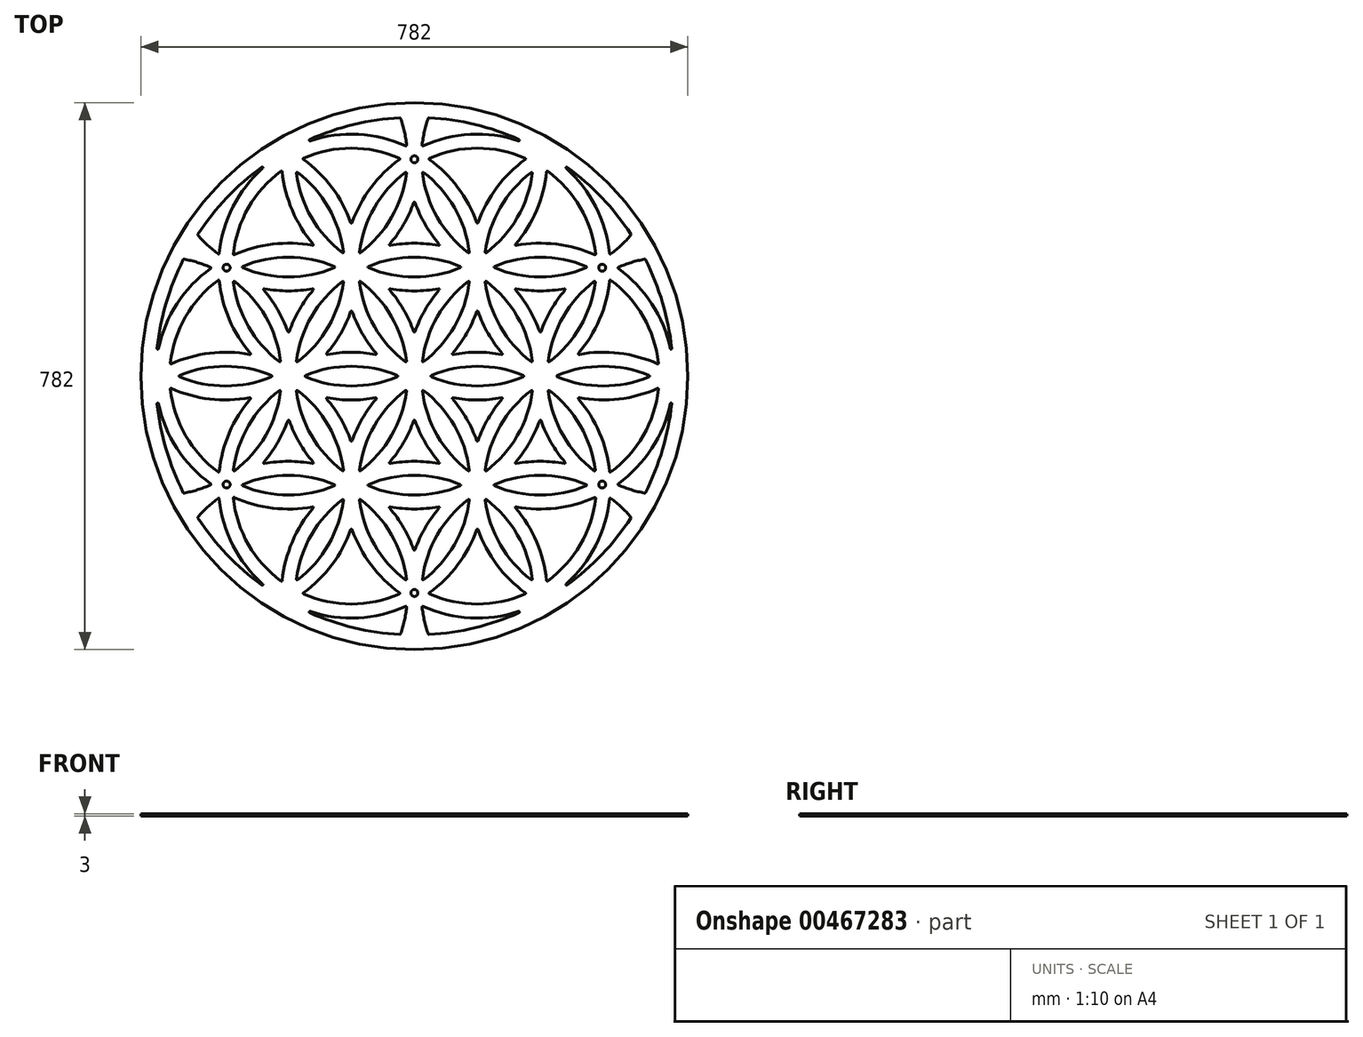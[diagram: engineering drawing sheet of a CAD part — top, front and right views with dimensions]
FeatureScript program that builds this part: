
annotation { "Feature Type Name" : "Feature", "Feature Type Description" : "" }
export const myFeature = defineFeature(function(context is Context, id is Id, definition is map)
    precondition{}
    {
        {
            var Q0;
            Q0=qCreatedBy(makeId("Top.planeOp"),FACE);
            var sketch = newSketch(context, id + "F0", { "sketchPlane" : qUnion([Q0])});
            skArc(sketch, "E0", {"start": v(-280.58, 137.05) * mm, "mid": v(-327.22, 85) * mm, "end": v(-348.98, 18.58) * mm});
            skArc(sketch, "E1", {"start": v(-291.41, 153.9) * mm, "mid": v(-339.34, 103.5) * mm, "end": v(-365.91, 39.2) * mm});
            skArc(sketch, "E2", {"start": v(-190.58, 292.94) * mm, "mid": v(-237.22, 240.88) * mm, "end": v(-258.98, 174.46) * mm});
            skArc(sketch, "E3", {"start": v(-21.41, 309.8) * mm, "mid": v(-62.1, 269.75) * mm, "end": v(-89.06, 219.43) * mm});
            skArc(sketch, "E4", {"start": v(257.58, 173.44) * mm, "mid": v(202.56, 188.66) * mm, "end": v(145.5, 186.84) * mm});
            skArc(sketch, "E5", {"start": v(179.06, 63.55) * mm, "mid": v(164.54, 95) * mm, "end": v(144.56, 123.3) * mm});
            skArc(sketch, "E6", {"start": v(-234.56, -32.6) * mm, "mid": v(-264.66, -81.1) * mm, "end": v(-279, -136.35) * mm});
            skArc(sketch, "E7", {"start": v(-192.97, -20.62) * mm, "mid": v(-237.22, -70.88) * mm, "end": v(-258.63, -134.35) * mm});
            skArc(sketch, "E8", {"start": v(155.66, 0.92) * mm, "mid": v(90, 14.12) * mm, "end": v(24.34, 0.92) * mm});
            skCircle(sketch, "E9", {"center": v(0, 0) * mm, "radius": 412 * mm});
            skArc(sketch, "E10", {"start": v(329.26, 167.2) * mm, "mid": v(310.1, 162.5) * mm, "end": v(291.6, 155.63) * mm});
            skArc(sketch, "E11", {"start": v(309.43, -201.55) * mm, "mid": v(295.78, -187.3) * mm, "end": v(280.58, -174.72) * mm});
            skArc(sketch, "E12", {"start": v(-214.5, 124.93) * mm, "mid": v(-180, 121.77) * mm, "end": v(-145.5, 124.93) * mm});
            skArc(sketch, "E13", {"start": v(-309.43, 201.55) * mm, "mid": v(-295.78, 187.3) * mm, "end": v(-280.58, 174.72) * mm});
            skArc(sketch, "E14", {"start": v(19.83, 368.75) * mm, "mid": v(14.3, 349.8) * mm, "end": v(11.02, 330.35) * mm});
            skArc(sketch, "E15", {"start": v(-20.83, 369.41) * mm, "mid": v(-86.68, 359.7) * mm, "end": v(-149.71, 338.36) * mm});
            skArc(sketch, "E16.trimOffspring", {"start": v(-329.26, -167.2) * mm, "mid": v(-310.1, -162.5) * mm, "end": v(-291.6, -155.63) * mm});
            skArc(sketch, "E17.trimOffspring", {"start": v(-19.83, -368.75) * mm, "mid": v(-14.3, -349.8) * mm, "end": v(-11.02, -330.35) * mm});
            skArc(sketch, "E18.trimOffspring", {"start": v(-189, 292.24) * mm, "mid": v(-174.66, 236.98) * mm, "end": v(-144.56, 188.47) * mm});
            skArc(sketch, "E19.trimOffspring", {"start": v(-12.42, 329.32) * mm, "mid": v(-80.04, 345.62) * mm, "end": v(-149, 336.5) * mm});
            skArc(sketch, "E20.trimOffspring", {"start": v(-11.02, 330.35) * mm, "mid": v(-14.3, 349.8) * mm, "end": v(-19.83, 368.75) * mm});
            skArc(sketch, "E21.trimOffspring", {"start": v(0.94, 248.22) * mm, "mid": v(15.46, 216.77) * mm, "end": v(35.44, 188.47) * mm});
            skArc(sketch, "E22.trimOffspring", {"start": v(-21.6, 311.52) * mm, "mid": v(-90, 325.88) * mm, "end": v(-158.4, 311.52) * mm});
            skArc(sketch, "E23.trimOffspring", {"start": v(11.37, 290.23) * mm, "mid": v(32.78, 226.77) * mm, "end": v(77.03, 176.5) * mm});
            skArc(sketch, "E24.trimOffspring", {"start": v(-12.97, 291.15) * mm, "mid": v(-57.22, 240.88) * mm, "end": v(-78.63, 177.42) * mm});
            skArc(sketch, "E25.trimOffspring", {"start": v(158.59, 309.8) * mm, "mid": v(117.9, 269.75) * mm, "end": v(90.94, 219.43) * mm});
            skArc(sketch, "E26.trimOffspring", {"start": v(167.03, 291.15) * mm, "mid": v(122.78, 240.88) * mm, "end": v(101.37, 177.42) * mm});
            skArc(sketch, "E27.trimOffspring", {"start": v(158.4, 311.52) * mm, "mid": v(90, 325.88) * mm, "end": v(21.6, 311.52) * mm});
            skArc(sketch, "E28.trimOffspring", {"start": v(-279, 136.35) * mm, "mid": v(-264.66, 81.1) * mm, "end": v(-234.56, 32.6) * mm});
            skArc(sketch, "E29.trimOffspring", {"start": v(-291.6, 155.63) * mm, "mid": v(-310.1, 162.5) * mm, "end": v(-329.26, 167.2) * mm});
            skArc(sketch, "E30.trimOffspring", {"start": v(-258.63, 134.35) * mm, "mid": v(-237.22, 70.88) * mm, "end": v(-192.97, 20.62) * mm});
            skArc(sketch, "E31.trimOffspring", {"start": v(-245.66, 154.96) * mm, "mid": v(-180, 141.77) * mm, "end": v(-114.34, 154.96) * mm});
            skArc(sketch, "E32.trimOffspring", {"start": v(280.58, 174.72) * mm, "mid": v(295.78, 187.3) * mm, "end": v(309.43, 201.55) * mm});
            skArc(sketch, "E33.trimOffspring", {"start": v(279, 175.42) * mm, "mid": v(259.3, 242.13) * mm, "end": v(216.91, 297.28) * mm});
            skArc(sketch, "E34.trimOffspring", {"start": v(257.03, 135.27) * mm, "mid": v(212.78, 85) * mm, "end": v(191.37, 21.54) * mm});
            skArc(sketch, "E35.trimOffspring", {"start": v(245.66, 156.8) * mm, "mid": v(180, 170) * mm, "end": v(114.34, 156.8) * mm});
            skArc(sketch, "E36.trimOffspring", {"start": v(215.44, 123.3) * mm, "mid": v(195.46, 95) * mm, "end": v(180.94, 63.55) * mm});
            skArc(sketch, "E37.trimOffspring", {"start": v(258.98, 174.46) * mm, "mid": v(237.22, 240.88) * mm, "end": v(190.58, 292.94) * mm});
            skArc(sketch, "E38.trimOffspring", {"start": v(235.5, -30.96) * mm, "mid": v(292.56, -32.77) * mm, "end": v(347.58, -17.56) * mm});
            skArc(sketch, "E39.trimOffspring", {"start": v(204.34, -0.92) * mm, "mid": v(270, -14.12) * mm, "end": v(335.66, -0.92) * mm});
            skArc(sketch, "E40.trimOffspring", {"start": v(234.56, 32.6) * mm, "mid": v(264.66, 81.1) * mm, "end": v(279, 136.35) * mm});
            skArc(sketch, "E41.trimOffspring", {"start": v(180.94, -63.55) * mm, "mid": v(195.46, -95) * mm, "end": v(215.44, -123.3) * mm});
            skArc(sketch, "E42.trimOffspring", {"start": v(192.97, 20.62) * mm, "mid": v(237.22, 70.88) * mm, "end": v(258.63, 134.35) * mm});
            skArc(sketch, "E43.trimOffspring", {"start": v(124.5, 30.96) * mm, "mid": v(90, 34.12) * mm, "end": v(55.5, 30.96) * mm});
            skArc(sketch, "E44.trimOffspring", {"start": v(125.44, -32.6) * mm, "mid": v(105.46, -60.88) * mm, "end": v(90.94, -92.34) * mm});
            skArc(sketch, "E45.trimOffspring", {"start": v(167.03, -20.62) * mm, "mid": v(122.78, -70.88) * mm, "end": v(101.37, -134.35) * mm});
            skArc(sketch, "E46.trimOffspring", {"start": v(168.63, 21.54) * mm, "mid": v(147.22, 85) * mm, "end": v(102.97, 135.27) * mm});
            skArc(sketch, "E47.trimOffspring", {"start": v(191.37, -21.54) * mm, "mid": v(212.78, -85) * mm, "end": v(257.03, -135.27) * mm});
            skArc(sketch, "E48.trimOffspring", {"start": v(145.5, 124.93) * mm, "mid": v(180, 121.77) * mm, "end": v(214.5, 124.93) * mm});
            skArc(sketch, "E49.trimOffspring", {"start": v(-348.98, -18.58) * mm, "mid": v(-327.22, -85) * mm, "end": v(-280.58, -137.05) * mm});
            skArc(sketch, "E50.trimOffspring", {"start": v(-335.66, -0.92) * mm, "mid": v(-270, -14.12) * mm, "end": v(-204.34, -0.92) * mm});
            skArc(sketch, "E51.trimOffspring", {"start": v(-347.58, -17.56) * mm, "mid": v(-292.56, -32.77) * mm, "end": v(-235.5, -30.96) * mm});
            skArc(sketch, "E52.trimOffspring", {"start": v(-365.91, -39.2) * mm, "mid": v(-339.34, -103.5) * mm, "end": v(-291.41, -153.9) * mm});
            skArc(sketch, "E53.trimOffspring", {"start": v(-145.5, 186.84) * mm, "mid": v(-202.56, 188.66) * mm, "end": v(-257.58, 173.44) * mm});
            skArc(sketch, "E54.trimOffspring", {"start": v(-77.03, 176.5) * mm, "mid": v(-32.78, 226.77) * mm, "end": v(-11.37, 290.23) * mm});
            skArc(sketch, "E55.trimOffspring", {"start": v(-168.63, 290.23) * mm, "mid": v(-147.22, 226.77) * mm, "end": v(-102.97, 176.5) * mm});
            skArc(sketch, "E56.trimOffspring", {"start": v(-34.5, 124.93) * mm, "mid": v(0, 121.77) * mm, "end": v(34.5, 124.93) * mm});
            skArc(sketch, "E57.trimOffspring", {"start": v(-78.63, 134.35) * mm, "mid": v(-57.22, 70.88) * mm, "end": v(-12.97, 20.62) * mm});
            skArc(sketch, "E58.trimOffspring", {"start": v(-89.06, 92.34) * mm, "mid": v(-74.54, 60.88) * mm, "end": v(-54.56, 32.6) * mm});
            skArc(sketch, "E59.trimOffspring", {"start": v(-102.97, 135.27) * mm, "mid": v(-147.22, 85) * mm, "end": v(-168.63, 21.54) * mm});
            skArc(sketch, "E60.trimOffspring", {"start": v(-114.34, 156.8) * mm, "mid": v(-180, 170) * mm, "end": v(-245.66, 156.8) * mm});
            skArc(sketch, "E61.trimOffspring", {"start": v(-144.56, 123.3) * mm, "mid": v(-164.54, 95) * mm, "end": v(-179.06, 63.55) * mm});
            skArc(sketch, "E62.trimOffspring", {"start": v(-180.94, 63.55) * mm, "mid": v(-195.46, 95) * mm, "end": v(-215.44, 123.3) * mm});
            skArc(sketch, "E63.trimOffspring", {"start": v(-35.44, 188.47) * mm, "mid": v(-15.46, 216.77) * mm, "end": v(-0.94, 248.22) * mm});
            skArc(sketch, "E64.trimOffspring", {"start": v(34.5, 186.84) * mm, "mid": v(0, 190) * mm, "end": v(-34.5, 186.84) * mm});
            skArc(sketch, "E65.trimOffspring", {"start": v(-90.94, 219.43) * mm, "mid": v(-117.9, 269.75) * mm, "end": v(-158.59, 309.8) * mm});
            skArc(sketch, "E66.trimOffspring", {"start": v(-101.37, 177.42) * mm, "mid": v(-122.78, 240.88) * mm, "end": v(-167.03, 291.15) * mm});
            skArc(sketch, "E67.trimOffspring", {"start": v(-65.66, 154.96) * mm, "mid": v(0, 141.77) * mm, "end": v(65.66, 154.96) * mm});
            skArc(sketch, "E68.trimOffspring", {"start": v(-216.91, 297.28) * mm, "mid": v(-259.3, 242.13) * mm, "end": v(-279, 175.42) * mm});
            skArc(sketch, "E69.trimOffspring", {"start": v(-218.17, 298.84) * mm, "mid": v(-268.18, 254.92) * mm, "end": v(-309.5, 202.75) * mm});
            skArc(sketch, "E70.trimOffspring", {"start": v(-330.34, 166.67) * mm, "mid": v(-354.85, 104.79) * mm, "end": v(-367.88, 39.52) * mm});
            skArc(sketch, "E71.trimOffspring", {"start": v(149, 336.5) * mm, "mid": v(80.04, 345.62) * mm, "end": v(12.42, 329.32) * mm});
            skArc(sketch, "E72.trimOffspring", {"start": v(149.71, 338.36) * mm, "mid": v(86.68, 359.7) * mm, "end": v(20.83, 369.41) * mm});
            skArc(sketch, "E73.trimOffspring", {"start": v(309.5, 202.75) * mm, "mid": v(268.18, 254.92) * mm, "end": v(218.17, 298.84) * mm});
            skArc(sketch, "E74.trimOffspring", {"start": v(90.94, 92.34) * mm, "mid": v(105.46, 60.88) * mm, "end": v(125.44, 32.6) * mm});
            skArc(sketch, "E75.trimOffspring", {"start": v(35.44, 123.3) * mm, "mid": v(15.46, 95) * mm, "end": v(0.94, 63.55) * mm});
            skArc(sketch, "E76.trimOffspring", {"start": v(89.06, 219.43) * mm, "mid": v(62.1, 269.75) * mm, "end": v(21.41, 309.8) * mm});
            skArc(sketch, "E77.trimOffspring", {"start": v(144.56, 188.47) * mm, "mid": v(174.66, 236.98) * mm, "end": v(189, 292.24) * mm});
            skArc(sketch, "E78.trimOffspring", {"start": v(102.97, 176.5) * mm, "mid": v(147.22, 226.77) * mm, "end": v(168.63, 290.23) * mm});
            skArc(sketch, "E79.trimOffspring", {"start": v(78.63, 177.42) * mm, "mid": v(57.22, 240.88) * mm, "end": v(12.97, 291.15) * mm});
            skArc(sketch, "E80.trimOffspring", {"start": v(114.34, 154.96) * mm, "mid": v(180, 141.77) * mm, "end": v(245.66, 154.96) * mm});
            skArc(sketch, "E81.trimOffspring", {"start": v(101.37, 134.35) * mm, "mid": v(122.78, 70.88) * mm, "end": v(167.03, 20.62) * mm});
            skArc(sketch, "E82.trimOffspring", {"start": v(77.03, 135.27) * mm, "mid": v(32.78, 85) * mm, "end": v(11.37, 21.54) * mm});
            skArc(sketch, "E83.trimOffspring", {"start": v(65.66, 156.8) * mm, "mid": v(0, 170) * mm, "end": v(-65.66, 156.8) * mm});
            skArc(sketch, "E84.trimOffspring", {"start": v(-367.88, -39.52) * mm, "mid": v(-354.85, -104.79) * mm, "end": v(-330.34, -166.67) * mm});
            skArc(sketch, "E85.trimOffspring", {"start": v(-235.5, 30.96) * mm, "mid": v(-292.56, 32.77) * mm, "end": v(-347.58, 17.56) * mm});
            skArc(sketch, "E86.trimOffspring", {"start": v(-124.5, -30.96) * mm, "mid": v(-90, -34.12) * mm, "end": v(-55.5, -30.96) * mm});
            skArc(sketch, "E87.trimOffspring", {"start": v(-179.06, -63.55) * mm, "mid": v(-164.54, -95) * mm, "end": v(-144.56, -123.3) * mm});
            skArc(sketch, "E88.trimOffspring", {"start": v(-125.44, 32.6) * mm, "mid": v(-105.46, 60.88) * mm, "end": v(-90.94, 92.34) * mm});
            skArc(sketch, "E89.trimOffspring", {"start": v(-204.34, 0.92) * mm, "mid": v(-270, 14.12) * mm, "end": v(-335.66, 0.92) * mm});
            skArc(sketch, "E90.trimOffspring", {"start": v(-191.37, 21.54) * mm, "mid": v(-212.78, 85) * mm, "end": v(-257.03, 135.27) * mm});
            skArc(sketch, "E91.trimOffspring", {"start": v(-167.03, 20.62) * mm, "mid": v(-122.78, 70.88) * mm, "end": v(-101.37, 134.35) * mm});
            skArc(sketch, "E92.trimOffspring", {"start": v(-155.66, -0.92) * mm, "mid": v(-90, -14.12) * mm, "end": v(-24.34, -0.92) * mm});
            skArc(sketch, "E93.trimOffspring", {"start": v(-168.63, -21.54) * mm, "mid": v(-147.22, -85) * mm, "end": v(-102.97, -135.27) * mm});
            skArc(sketch, "E94.trimOffspring", {"start": v(335.66, 0.92) * mm, "mid": v(270, 14.12) * mm, "end": v(204.34, 0.92) * mm});
            skArc(sketch, "E95.trimOffspring", {"start": v(347.58, 17.56) * mm, "mid": v(292.56, 32.77) * mm, "end": v(235.5, 30.96) * mm});
            skArc(sketch, "E96.trimOffspring", {"start": v(348.98, 18.58) * mm, "mid": v(327.22, 85) * mm, "end": v(280.58, 137.05) * mm});
            skArc(sketch, "E97.trimOffspring", {"start": v(365.91, 39.2) * mm, "mid": v(339.34, 103.5) * mm, "end": v(291.41, 153.9) * mm});
            skArc(sketch, "E98.trimOffspring", {"start": v(367.88, 39.52) * mm, "mid": v(354.85, 104.79) * mm, "end": v(330.34, 166.67) * mm});
            skArc(sketch, "E99.trimOffspring", {"start": v(-11.37, 21.54) * mm, "mid": v(-32.78, 85) * mm, "end": v(-77.03, 135.27) * mm});
            skArc(sketch, "E100.trimOffspring", {"start": v(-0.94, 63.55) * mm, "mid": v(-15.46, 95) * mm, "end": v(-35.44, 123.3) * mm});
            skArc(sketch, "E101.trimOffspring", {"start": v(12.97, 20.62) * mm, "mid": v(57.22, 70.88) * mm, "end": v(78.63, 134.35) * mm});
            skArc(sketch, "E102.trimOffspring", {"start": v(54.56, 32.6) * mm, "mid": v(74.54, 60.88) * mm, "end": v(89.06, 92.34) * mm});
            skArc(sketch, "E103.trimOffspring", {"start": v(24.34, -0.92) * mm, "mid": v(90, -14.12) * mm, "end": v(155.66, -0.92) * mm});
            skArc(sketch, "E104.trimOffspring", {"start": v(55.5, -30.96) * mm, "mid": v(90, -34.12) * mm, "end": v(124.5, -30.96) * mm});
            skArc(sketch, "E105.trimOffspring", {"start": v(0.94, -63.55) * mm, "mid": v(15.46, -95) * mm, "end": v(35.44, -123.3) * mm});
            skArc(sketch, "E106.trimOffspring", {"start": v(11.37, -21.54) * mm, "mid": v(32.78, -85) * mm, "end": v(77.03, -135.27) * mm});
            skArc(sketch, "E107.trimOffspring", {"start": v(-12.97, -20.62) * mm, "mid": v(-57.22, -70.88) * mm, "end": v(-78.63, -134.35) * mm});
            skArc(sketch, "E108.trimOffspring", {"start": v(-54.56, -32.6) * mm, "mid": v(-74.54, -60.88) * mm, "end": v(-89.06, -92.34) * mm});
            skArc(sketch, "E109.trimOffspring", {"start": v(-24.34, 0.92) * mm, "mid": v(-90, 14.12) * mm, "end": v(-155.66, 0.92) * mm});
            skArc(sketch, "E110.trimOffspring", {"start": v(-55.5, 30.96) * mm, "mid": v(-90, 34.12) * mm, "end": v(-124.5, 30.96) * mm});
            skArc(sketch, "E111.trimOffspring", {"start": v(-309.5, -202.75) * mm, "mid": v(-268.18, -254.92) * mm, "end": v(-218.17, -298.84) * mm});
            skArc(sketch, "E112.trimOffspring", {"start": v(-279, -175.42) * mm, "mid": v(-259.3, -242.13) * mm, "end": v(-216.91, -297.28) * mm});
            skArc(sketch, "E113.trimOffspring", {"start": v(-280.58, -174.72) * mm, "mid": v(-295.78, -187.3) * mm, "end": v(-309.43, -201.55) * mm});
            skArc(sketch, "E114.trimOffspring", {"start": v(-215.44, -123.3) * mm, "mid": v(-195.46, -95) * mm, "end": v(-180.94, -63.55) * mm});
            skArc(sketch, "E115.trimOffspring", {"start": v(-257.03, -135.27) * mm, "mid": v(-212.78, -85) * mm, "end": v(-191.37, -21.54) * mm});
            skArc(sketch, "E116.trimOffspring", {"start": v(-257.58, -173.44) * mm, "mid": v(-202.56, -188.66) * mm, "end": v(-145.5, -186.84) * mm});
            skArc(sketch, "E117.trimOffspring", {"start": v(-258.98, -174.46) * mm, "mid": v(-237.22, -240.88) * mm, "end": v(-190.58, -292.94) * mm});
            skArc(sketch, "E118.trimOffspring", {"start": v(-245.66, -156.8) * mm, "mid": v(-180, -170) * mm, "end": v(-114.34, -156.8) * mm});
            skArc(sketch, "E119.trimOffspring", {"start": v(-167.03, -291.15) * mm, "mid": v(-122.78, -240.88) * mm, "end": v(-101.37, -177.42) * mm});
            skArc(sketch, "E120.trimOffspring", {"start": v(-149, -336.5) * mm, "mid": v(-80.04, -345.62) * mm, "end": v(-12.42, -329.32) * mm});
            skArc(sketch, "E121.trimOffspring", {"start": v(-149.71, -338.36) * mm, "mid": v(-86.68, -359.7) * mm, "end": v(-20.83, -369.41) * mm});
            skArc(sketch, "E122.trimOffspring", {"start": v(-158.59, -309.8) * mm, "mid": v(-117.9, -269.75) * mm, "end": v(-90.94, -219.43) * mm});
            skArc(sketch, "E123.trimOffspring", {"start": v(-158.4, -311.52) * mm, "mid": v(-90, -325.88) * mm, "end": v(-21.6, -311.52) * mm});
            skArc(sketch, "E124.trimOffspring", {"start": v(-114.34, -154.96) * mm, "mid": v(-180, -141.77) * mm, "end": v(-245.66, -154.96) * mm});
            skArc(sketch, "E125.trimOffspring", {"start": v(-145.5, -124.93) * mm, "mid": v(-180, -121.77) * mm, "end": v(-214.5, -124.93) * mm});
            skArc(sketch, "E126.trimOffspring", {"start": v(-101.37, -134.35) * mm, "mid": v(-122.78, -70.88) * mm, "end": v(-167.03, -20.62) * mm});
            skArc(sketch, "E127.trimOffspring", {"start": v(-90.94, -92.34) * mm, "mid": v(-105.46, -60.88) * mm, "end": v(-125.44, -32.6) * mm});
            skArc(sketch, "E128.trimOffspring", {"start": v(-77.03, -135.27) * mm, "mid": v(-32.78, -85) * mm, "end": v(-11.37, -21.54) * mm});
            skArc(sketch, "E129.trimOffspring", {"start": v(-35.44, -123.3) * mm, "mid": v(-15.46, -95) * mm, "end": v(-0.94, -63.55) * mm});
            skArc(sketch, "E130.trimOffspring", {"start": v(-65.66, -156.8) * mm, "mid": v(0, -170) * mm, "end": v(65.66, -156.8) * mm});
            skArc(sketch, "E131.trimOffspring", {"start": v(-34.5, -186.84) * mm, "mid": v(0, -190) * mm, "end": v(34.5, -186.84) * mm});
            skArc(sketch, "E132.trimOffspring", {"start": v(-78.63, -177.42) * mm, "mid": v(-57.22, -240.88) * mm, "end": v(-12.97, -291.15) * mm});
            skArc(sketch, "E133.trimOffspring", {"start": v(-89.06, -219.43) * mm, "mid": v(-62.1, -269.75) * mm, "end": v(-21.41, -309.8) * mm});
            skArc(sketch, "E134.trimOffspring", {"start": v(-102.97, -176.5) * mm, "mid": v(-147.22, -226.77) * mm, "end": v(-168.63, -290.23) * mm});
            skArc(sketch, "E135.trimOffspring", {"start": v(-144.56, -188.47) * mm, "mid": v(-174.66, -236.98) * mm, "end": v(-189, -292.24) * mm});
            skArc(sketch, "E136.trimOffspring", {"start": v(65.66, -154.96) * mm, "mid": v(0, -141.77) * mm, "end": v(-65.66, -154.96) * mm});
            skArc(sketch, "E137.trimOffspring", {"start": v(34.5, -124.93) * mm, "mid": v(0, -121.77) * mm, "end": v(-34.5, -124.93) * mm});
            skArc(sketch, "E138.trimOffspring", {"start": v(78.63, -134.35) * mm, "mid": v(57.22, -70.88) * mm, "end": v(12.97, -20.62) * mm});
            skArc(sketch, "E139.trimOffspring", {"start": v(89.06, -92.34) * mm, "mid": v(74.54, -60.88) * mm, "end": v(54.56, -32.6) * mm});
            skArc(sketch, "E140.trimOffspring", {"start": v(102.97, -135.27) * mm, "mid": v(147.22, -85) * mm, "end": v(168.63, -21.54) * mm});
            skArc(sketch, "E141.trimOffspring", {"start": v(144.56, -123.3) * mm, "mid": v(164.54, -95) * mm, "end": v(179.06, -63.55) * mm});
            skArc(sketch, "E142.trimOffspring", {"start": v(114.34, -156.8) * mm, "mid": v(180, -170) * mm, "end": v(245.66, -156.8) * mm});
            skArc(sketch, "E143.trimOffspring", {"start": v(145.5, -186.84) * mm, "mid": v(202.56, -188.66) * mm, "end": v(257.58, -173.44) * mm});
            skArc(sketch, "E144.trimOffspring", {"start": v(101.37, -177.42) * mm, "mid": v(122.78, -240.88) * mm, "end": v(167.03, -291.15) * mm});
            skArc(sketch, "E145.trimOffspring", {"start": v(90.94, -219.43) * mm, "mid": v(117.9, -269.75) * mm, "end": v(158.59, -309.8) * mm});
            skArc(sketch, "E146.trimOffspring", {"start": v(77.03, -176.5) * mm, "mid": v(32.78, -226.77) * mm, "end": v(11.37, -290.23) * mm});
            skArc(sketch, "E147.trimOffspring", {"start": v(35.44, -188.47) * mm, "mid": v(15.46, -216.77) * mm, "end": v(0.94, -248.22) * mm});
            skArc(sketch, "E148.trimOffspring", {"start": v(214.5, -124.93) * mm, "mid": v(180, -121.77) * mm, "end": v(145.5, -124.93) * mm});
            skArc(sketch, "E149.trimOffspring", {"start": v(280.58, -137.05) * mm, "mid": v(327.22, -85) * mm, "end": v(348.98, -18.58) * mm});
            skArc(sketch, "E150.trimOffspring", {"start": v(279, -136.35) * mm, "mid": v(264.66, -81.1) * mm, "end": v(234.56, -32.6) * mm});
            skArc(sketch, "E151.trimOffspring", {"start": v(258.63, -134.35) * mm, "mid": v(237.22, -70.88) * mm, "end": v(192.97, -20.62) * mm});
            skArc(sketch, "E152.trimOffspring", {"start": v(245.66, -154.96) * mm, "mid": v(180, -141.77) * mm, "end": v(114.34, -154.96) * mm});
            skArc(sketch, "E153.trimOffspring", {"start": v(291.41, -153.9) * mm, "mid": v(339.34, -103.5) * mm, "end": v(365.91, -39.2) * mm});
            skArc(sketch, "E154.trimOffspring", {"start": v(291.6, -155.63) * mm, "mid": v(310.1, -162.5) * mm, "end": v(329.26, -167.2) * mm});
            skArc(sketch, "E155.trimOffspring", {"start": v(330.34, -166.67) * mm, "mid": v(354.85, -104.79) * mm, "end": v(367.88, -39.52) * mm});
            skArc(sketch, "E156.trimOffspring", {"start": v(168.63, -290.23) * mm, "mid": v(147.22, -226.77) * mm, "end": v(102.97, -176.5) * mm});
            skArc(sketch, "E157.trimOffspring", {"start": v(190.58, -292.94) * mm, "mid": v(237.22, -240.88) * mm, "end": v(258.98, -174.46) * mm});
            skArc(sketch, "E158.trimOffspring", {"start": v(189, -292.24) * mm, "mid": v(174.66, -236.98) * mm, "end": v(144.56, -188.47) * mm});
            skArc(sketch, "E159.trimOffspring", {"start": v(218.17, -298.84) * mm, "mid": v(268.18, -254.92) * mm, "end": v(309.5, -202.75) * mm});
            skArc(sketch, "E160.trimOffspring", {"start": v(216.91, -297.28) * mm, "mid": v(259.3, -242.13) * mm, "end": v(279, -175.42) * mm});
            skArc(sketch, "E161.trimOffspring", {"start": v(20.83, -369.41) * mm, "mid": v(86.68, -359.7) * mm, "end": v(149.71, -338.36) * mm});
            skArc(sketch, "E162.trimOffspring", {"start": v(-0.94, -248.22) * mm, "mid": v(-15.46, -216.77) * mm, "end": v(-35.44, -188.47) * mm});
            skArc(sketch, "E163.trimOffspring", {"start": v(12.42, -329.32) * mm, "mid": v(80.04, -345.62) * mm, "end": v(149, -336.5) * mm});
            skArc(sketch, "E164.trimOffspring", {"start": v(21.6, -311.52) * mm, "mid": v(90, -325.88) * mm, "end": v(158.4, -311.52) * mm});
            skArc(sketch, "E165.trimOffspring", {"start": v(21.41, -309.8) * mm, "mid": v(62.1, -269.75) * mm, "end": v(89.06, -219.43) * mm});
            skArc(sketch, "E166.trimOffspring", {"start": v(11.02, -330.35) * mm, "mid": v(14.3, -349.8) * mm, "end": v(19.83, -368.75) * mm});
            skArc(sketch, "E167.trimOffspring", {"start": v(-11.37, -290.23) * mm, "mid": v(-32.78, -226.77) * mm, "end": v(-77.03, -176.5) * mm});
            skArc(sketch, "E168.trimOffspring", {"start": v(12.97, -291.15) * mm, "mid": v(57.22, -240.88) * mm, "end": v(78.63, -177.42) * mm});
            skArc(sketch, "E169.filletArc", {"start": v(149.71, -338.36) * mm, "mid": v(150.24, -337.08) * mm, "end": v(149, -336.5) * mm});
            skPoint(sketch, "E170.visualSharp", {"position": v(20.09, -369.45) * mm});
            skArc(sketch, "E170.filletArc", {"start": v(19.83, -368.75) * mm, "mid": v(20.22, -369.25) * mm, "end": v(20.83, -369.41) * mm});
            skPoint(sketch, "E171.visualSharp", {"position": v(10.84, -328.6) * mm});
            skArc(sketch, "E171.filletArc", {"start": v(12.42, -329.32) * mm, "mid": v(11.42, -329.43) * mm, "end": v(11.02, -330.35) * mm});
            skArc(sketch, "E172.filletArc", {"start": v(216.91, -297.28) * mm, "mid": v(216.8, -298.66) * mm, "end": v(218.17, -298.84) * mm});
            skPoint(sketch, "E173.visualSharp", {"position": v(309.91, -202.12) * mm});
            skArc(sketch, "E173.filletArc", {"start": v(309.5, -202.75) * mm, "mid": v(309.67, -202.14) * mm, "end": v(309.43, -201.55) * mm});
            skPoint(sketch, "E174.visualSharp", {"position": v(279.16, -173.69) * mm});
            skArc(sketch, "E174.filletArc", {"start": v(280.58, -174.72) * mm, "mid": v(279.58, -174.6) * mm, "end": v(279, -175.42) * mm});
            skPoint(sketch, "E175.visualSharp", {"position": v(290, -154.92) * mm});
            skArc(sketch, "E175.filletArc", {"start": v(291.41, -153.9) * mm, "mid": v(291, -154.82) * mm, "end": v(291.6, -155.63) * mm});
            skPoint(sketch, "E176.visualSharp", {"position": v(330, -167.33) * mm});
            skArc(sketch, "E176.filletArc", {"start": v(329.26, -167.2) * mm, "mid": v(329.89, -167.11) * mm, "end": v(330.34, -166.67) * mm});
            skArc(sketch, "E177.filletArc", {"start": v(367.88, -39.52) * mm, "mid": v(367.05, -38.43) * mm, "end": v(365.91, -39.2) * mm});
            skArc(sketch, "E178.filletArc", {"start": v(365.91, 39.2) * mm, "mid": v(367.05, 38.43) * mm, "end": v(367.88, 39.52) * mm});
            skPoint(sketch, "E179.visualSharp", {"position": v(330, 167.33) * mm});
            skArc(sketch, "E179.filletArc", {"start": v(330.34, 166.67) * mm, "mid": v(329.89, 167.11) * mm, "end": v(329.26, 167.2) * mm});
            skPoint(sketch, "E180.visualSharp", {"position": v(290, 154.92) * mm});
            skArc(sketch, "E180.filletArc", {"start": v(291.6, 155.63) * mm, "mid": v(291, 154.82) * mm, "end": v(291.41, 153.9) * mm});
            skPoint(sketch, "E181.visualSharp", {"position": v(279.16, 173.69) * mm});
            skArc(sketch, "E181.filletArc", {"start": v(279, 175.42) * mm, "mid": v(279.58, 174.6) * mm, "end": v(280.58, 174.72) * mm});
            skPoint(sketch, "E182.visualSharp", {"position": v(309.91, 202.12) * mm});
            skArc(sketch, "E182.filletArc", {"start": v(309.43, 201.55) * mm, "mid": v(309.67, 202.14) * mm, "end": v(309.5, 202.75) * mm});
            skArc(sketch, "E183.filletArc", {"start": v(218.17, 298.84) * mm, "mid": v(216.8, 298.66) * mm, "end": v(216.91, 297.28) * mm});
            skArc(sketch, "E184.filletArc", {"start": v(149, 336.5) * mm, "mid": v(150.24, 337.08) * mm, "end": v(149.71, 338.36) * mm});
            skPoint(sketch, "E185.visualSharp", {"position": v(20.09, 369.45) * mm});
            skArc(sketch, "E185.filletArc", {"start": v(20.83, 369.41) * mm, "mid": v(20.22, 369.25) * mm, "end": v(19.83, 368.75) * mm});
            skPoint(sketch, "E186.visualSharp", {"position": v(10.84, 328.6) * mm});
            skArc(sketch, "E186.filletArc", {"start": v(11.02, 330.35) * mm, "mid": v(11.42, 329.43) * mm, "end": v(12.42, 329.32) * mm});
            skPoint(sketch, "E187.visualSharp", {"position": v(-20.09, 369.45) * mm});
            skArc(sketch, "E187.filletArc", {"start": v(-19.83, 368.75) * mm, "mid": v(-20.22, 369.25) * mm, "end": v(-20.83, 369.41) * mm});
            skPoint(sketch, "E188.visualSharp", {"position": v(-10.84, 328.6) * mm});
            skArc(sketch, "E188.filletArc", {"start": v(-12.42, 329.32) * mm, "mid": v(-11.42, 329.43) * mm, "end": v(-11.02, 330.35) * mm});
            skArc(sketch, "E189.filletArc", {"start": v(-149.71, 338.36) * mm, "mid": v(-150.24, 337.08) * mm, "end": v(-149, 336.5) * mm});
            skArc(sketch, "E190.filletArc", {"start": v(-216.91, 297.28) * mm, "mid": v(-216.8, 298.66) * mm, "end": v(-218.17, 298.84) * mm});
            skPoint(sketch, "E191.visualSharp", {"position": v(-309.91, 202.12) * mm});
            skArc(sketch, "E191.filletArc", {"start": v(-309.5, 202.75) * mm, "mid": v(-309.67, 202.14) * mm, "end": v(-309.43, 201.55) * mm});
            skPoint(sketch, "E192.visualSharp", {"position": v(-279.16, 173.69) * mm});
            skArc(sketch, "E192.filletArc", {"start": v(-280.58, 174.72) * mm, "mid": v(-279.58, 174.6) * mm, "end": v(-279, 175.42) * mm});
            skPoint(sketch, "E193.visualSharp", {"position": v(-290, 154.92) * mm});
            skArc(sketch, "E193.filletArc", {"start": v(-291.41, 153.9) * mm, "mid": v(-291, 154.82) * mm, "end": v(-291.6, 155.63) * mm});
            skPoint(sketch, "E194.visualSharp", {"position": v(-330, 167.33) * mm});
            skArc(sketch, "E194.filletArc", {"start": v(-329.26, 167.2) * mm, "mid": v(-329.89, 167.11) * mm, "end": v(-330.34, 166.67) * mm});
            skArc(sketch, "E195.filletArc", {"start": v(-367.88, 39.52) * mm, "mid": v(-367.05, 38.43) * mm, "end": v(-365.91, 39.2) * mm});
            skArc(sketch, "E196.filletArc", {"start": v(-365.91, -39.2) * mm, "mid": v(-367.05, -38.43) * mm, "end": v(-367.88, -39.52) * mm});
            skPoint(sketch, "E197.visualSharp", {"position": v(-290, -154.92) * mm});
            skArc(sketch, "E197.filletArc", {"start": v(-291.6, -155.63) * mm, "mid": v(-291, -154.82) * mm, "end": v(-291.41, -153.9) * mm});
            skPoint(sketch, "E198.visualSharp", {"position": v(-330, -167.33) * mm});
            skArc(sketch, "E198.filletArc", {"start": v(-330.34, -166.67) * mm, "mid": v(-329.89, -167.11) * mm, "end": v(-329.26, -167.2) * mm});
            skPoint(sketch, "E199.visualSharp", {"position": v(-279.16, -173.69) * mm});
            skArc(sketch, "E199.filletArc", {"start": v(-279, -175.42) * mm, "mid": v(-279.58, -174.6) * mm, "end": v(-280.58, -174.72) * mm});
            skPoint(sketch, "E200.visualSharp", {"position": v(-309.91, -202.12) * mm});
            skArc(sketch, "E200.filletArc", {"start": v(-309.43, -201.55) * mm, "mid": v(-309.67, -202.14) * mm, "end": v(-309.5, -202.75) * mm});
            skArc(sketch, "E201.filletArc", {"start": v(-218.17, -298.84) * mm, "mid": v(-216.8, -298.66) * mm, "end": v(-216.91, -297.28) * mm});
            skArc(sketch, "E202.filletArc", {"start": v(-149, -336.5) * mm, "mid": v(-150.24, -337.08) * mm, "end": v(-149.71, -338.36) * mm});
            skPoint(sketch, "E203.visualSharp", {"position": v(-20.09, -369.45) * mm});
            skArc(sketch, "E203.filletArc", {"start": v(-20.83, -369.41) * mm, "mid": v(-20.22, -369.25) * mm, "end": v(-19.83, -368.75) * mm});
            skPoint(sketch, "E204.visualSharp", {"position": v(-10.84, -328.6) * mm});
            skArc(sketch, "E204.filletArc", {"start": v(-11.02, -330.35) * mm, "mid": v(-11.42, -329.43) * mm, "end": v(-12.42, -329.32) * mm});
            skPoint(sketch, "E205.visualSharp", {"position": v(20, -310.8) * mm});
            skArc(sketch, "E205.filletArc", {"start": v(21.41, -309.8) * mm, "mid": v(21, -310.7) * mm, "end": v(21.6, -311.52) * mm});
            skPoint(sketch, "E206.visualSharp", {"position": v(160, -310.8) * mm});
            skArc(sketch, "E206.filletArc", {"start": v(158.4, -311.52) * mm, "mid": v(159, -310.7) * mm, "end": v(158.59, -309.8) * mm});
            skPoint(sketch, "E207.visualSharp", {"position": v(90, -216.71) * mm});
            skArc(sketch, "E207.filletArc", {"start": v(90.94, -219.43) * mm, "mid": v(90, -218.77) * mm, "end": v(89.06, -219.43) * mm});
            skPoint(sketch, "E208.visualSharp", {"position": v(11.09, -292.56) * mm});
            skArc(sketch, "E208.filletArc", {"start": v(11.37, -290.23) * mm, "mid": v(11.86, -291.22) * mm, "end": v(12.97, -291.15) * mm});
            skPoint(sketch, "E209.visualSharp", {"position": v(78.91, -175.1) * mm});
            skArc(sketch, "E209.filletArc", {"start": v(78.63, -177.42) * mm, "mid": v(78.14, -176.43) * mm, "end": v(77.03, -176.5) * mm});
            skPoint(sketch, "E210.visualSharp", {"position": v(101.09, -175.1) * mm});
            skArc(sketch, "E210.filletArc", {"start": v(102.97, -176.5) * mm, "mid": v(101.86, -176.43) * mm, "end": v(101.37, -177.42) * mm});
            skPoint(sketch, "E211.visualSharp", {"position": v(168.91, -292.56) * mm});
            skArc(sketch, "E211.filletArc", {"start": v(167.03, -291.15) * mm, "mid": v(168.14, -291.22) * mm, "end": v(168.63, -290.23) * mm});
            skPoint(sketch, "E212.visualSharp", {"position": v(0, -250.94) * mm});
            skArc(sketch, "E212.filletArc", {"start": v(-0.94, -248.22) * mm, "mid": v(0, -248.89) * mm, "end": v(0.94, -248.22) * mm});
            skPoint(sketch, "E213.visualSharp", {"position": v(-37.32, -186.3) * mm});
            skArc(sketch, "E213.filletArc", {"start": v(-34.5, -186.84) * mm, "mid": v(-35.54, -187.33) * mm, "end": v(-35.44, -188.47) * mm});
            skPoint(sketch, "E214.visualSharp", {"position": v(37.32, -186.3) * mm});
            skArc(sketch, "E214.filletArc", {"start": v(35.44, -188.47) * mm, "mid": v(35.54, -187.33) * mm, "end": v(34.5, -186.84) * mm});
            skPoint(sketch, "E215.visualSharp", {"position": v(-11.09, -292.56) * mm});
            skArc(sketch, "E215.filletArc", {"start": v(-12.97, -291.15) * mm, "mid": v(-11.86, -291.22) * mm, "end": v(-11.37, -290.23) * mm});
            skPoint(sketch, "E216.visualSharp", {"position": v(-78.91, -175.1) * mm});
            skArc(sketch, "E216.filletArc", {"start": v(-77.03, -176.5) * mm, "mid": v(-78.14, -176.43) * mm, "end": v(-78.63, -177.42) * mm});
            skPoint(sketch, "E217.visualSharp", {"position": v(-20, -310.8) * mm});
            skArc(sketch, "E217.filletArc", {"start": v(-21.6, -311.52) * mm, "mid": v(-21, -310.7) * mm, "end": v(-21.41, -309.8) * mm});
            skPoint(sketch, "E218.visualSharp", {"position": v(-160, -310.8) * mm});
            skArc(sketch, "E218.filletArc", {"start": v(-158.59, -309.8) * mm, "mid": v(-159, -310.7) * mm, "end": v(-158.4, -311.52) * mm});
            skPoint(sketch, "E219.visualSharp", {"position": v(-90, -216.71) * mm});
            skArc(sketch, "E219.filletArc", {"start": v(-89.06, -219.43) * mm, "mid": v(-90, -218.77) * mm, "end": v(-90.94, -219.43) * mm});
            skPoint(sketch, "E220.visualSharp", {"position": v(-168.91, -292.56) * mm});
            skArc(sketch, "E220.filletArc", {"start": v(-168.63, -290.23) * mm, "mid": v(-168.14, -291.22) * mm, "end": v(-167.03, -291.15) * mm});
            skPoint(sketch, "E221.visualSharp", {"position": v(-101.09, -175.1) * mm});
            skArc(sketch, "E221.filletArc", {"start": v(-101.37, -177.42) * mm, "mid": v(-101.86, -176.43) * mm, "end": v(-102.97, -176.5) * mm});
            skPoint(sketch, "E222.visualSharp", {"position": v(-189.16, -293.97) * mm});
            skArc(sketch, "E222.filletArc", {"start": v(-190.58, -292.94) * mm, "mid": v(-189.58, -293.05) * mm, "end": v(-189, -292.24) * mm});
            skPoint(sketch, "E223.visualSharp", {"position": v(-259.16, -172.72) * mm});
            skArc(sketch, "E223.filletArc", {"start": v(-257.58, -173.44) * mm, "mid": v(-258.58, -173.54) * mm, "end": v(-258.98, -174.46) * mm});
            skPoint(sketch, "E224.visualSharp", {"position": v(-142.68, -186.3) * mm});
            skArc(sketch, "E224.filletArc", {"start": v(-144.56, -188.47) * mm, "mid": v(-144.46, -187.33) * mm, "end": v(-145.5, -186.84) * mm});
            skPoint(sketch, "E225.visualSharp", {"position": v(142.68, -186.3) * mm});
            skArc(sketch, "E225.filletArc", {"start": v(145.5, -186.84) * mm, "mid": v(144.46, -187.33) * mm, "end": v(144.56, -188.47) * mm});
            skPoint(sketch, "E226.visualSharp", {"position": v(189.16, -293.97) * mm});
            skArc(sketch, "E226.filletArc", {"start": v(189, -292.24) * mm, "mid": v(189.58, -293.05) * mm, "end": v(190.58, -292.94) * mm});
            skPoint(sketch, "E227.visualSharp", {"position": v(259.16, -172.72) * mm});
            skArc(sketch, "E227.filletArc", {"start": v(258.98, -174.46) * mm, "mid": v(258.58, -173.54) * mm, "end": v(257.58, -173.44) * mm});
            skPoint(sketch, "E228.visualSharp", {"position": v(-247.82, -155.88) * mm});
            skArc(sketch, "E228.filletArc", {"start": v(-245.66, -154.96) * mm, "mid": v(-246.28, -155.88) * mm, "end": v(-245.66, -156.8) * mm});
            skPoint(sketch, "E229.visualSharp", {"position": v(-112.18, -155.88) * mm});
            skArc(sketch, "E229.filletArc", {"start": v(-114.34, -156.8) * mm, "mid": v(-113.72, -155.88) * mm, "end": v(-114.34, -154.96) * mm});
            skPoint(sketch, "E230.visualSharp", {"position": v(-67.82, -155.88) * mm});
            skArc(sketch, "E230.filletArc", {"start": v(-65.66, -154.96) * mm, "mid": v(-66.28, -155.88) * mm, "end": v(-65.66, -156.8) * mm});
            skPoint(sketch, "E231.visualSharp", {"position": v(67.82, -155.88) * mm});
            skArc(sketch, "E231.filletArc", {"start": v(65.66, -156.8) * mm, "mid": v(66.28, -155.88) * mm, "end": v(65.66, -154.96) * mm});
            skPoint(sketch, "E232.visualSharp", {"position": v(112.18, -155.88) * mm});
            skArc(sketch, "E232.filletArc", {"start": v(114.34, -154.96) * mm, "mid": v(113.72, -155.88) * mm, "end": v(114.34, -156.8) * mm});
            skPoint(sketch, "E233.visualSharp", {"position": v(247.82, -155.88) * mm});
            skArc(sketch, "E233.filletArc", {"start": v(245.66, -156.8) * mm, "mid": v(246.28, -155.88) * mm, "end": v(245.66, -154.96) * mm});
            skPoint(sketch, "E234.visualSharp", {"position": v(191.09, -19.2) * mm});
            skArc(sketch, "E234.filletArc", {"start": v(192.97, -20.62) * mm, "mid": v(191.86, -20.55) * mm, "end": v(191.37, -21.54) * mm});
            skPoint(sketch, "E235.visualSharp", {"position": v(258.91, -136.68) * mm});
            skArc(sketch, "E235.filletArc", {"start": v(257.03, -135.27) * mm, "mid": v(258.14, -135.34) * mm, "end": v(258.63, -134.35) * mm});
            skPoint(sketch, "E236.visualSharp", {"position": v(217.32, -125.47) * mm});
            skArc(sketch, "E236.filletArc", {"start": v(214.5, -124.93) * mm, "mid": v(215.54, -124.44) * mm, "end": v(215.44, -123.3) * mm});
            skPoint(sketch, "E237.visualSharp", {"position": v(180, -60.83) * mm});
            skArc(sketch, "E237.filletArc", {"start": v(180.94, -63.55) * mm, "mid": v(180, -62.88) * mm, "end": v(179.06, -63.55) * mm});
            skPoint(sketch, "E238.visualSharp", {"position": v(142.68, -125.47) * mm});
            skArc(sketch, "E238.filletArc", {"start": v(144.56, -123.3) * mm, "mid": v(144.46, -124.44) * mm, "end": v(145.5, -124.93) * mm});
            skPoint(sketch, "E239.visualSharp", {"position": v(168.91, -19.2) * mm});
            skArc(sketch, "E239.filletArc", {"start": v(168.63, -21.54) * mm, "mid": v(168.14, -20.55) * mm, "end": v(167.03, -20.62) * mm});
            skPoint(sketch, "E240.visualSharp", {"position": v(101.09, -136.68) * mm});
            skArc(sketch, "E240.filletArc", {"start": v(101.37, -134.35) * mm, "mid": v(101.86, -135.34) * mm, "end": v(102.97, -135.27) * mm});
            skPoint(sketch, "E241.visualSharp", {"position": v(90, -95.06) * mm});
            skArc(sketch, "E241.filletArc", {"start": v(89.06, -92.34) * mm, "mid": v(90, -93) * mm, "end": v(90.94, -92.34) * mm});
            skPoint(sketch, "E242.visualSharp", {"position": v(52.68, -30.41) * mm});
            skArc(sketch, "E242.filletArc", {"start": v(55.5, -30.96) * mm, "mid": v(54.46, -31.44) * mm, "end": v(54.56, -32.6) * mm});
            skPoint(sketch, "E243.visualSharp", {"position": v(127.32, -30.41) * mm});
            skArc(sketch, "E243.filletArc", {"start": v(125.44, -32.6) * mm, "mid": v(125.54, -31.44) * mm, "end": v(124.5, -30.96) * mm});
            skPoint(sketch, "E244.visualSharp", {"position": v(11.09, -19.2) * mm});
            skArc(sketch, "E244.filletArc", {"start": v(12.97, -20.62) * mm, "mid": v(11.86, -20.55) * mm, "end": v(11.37, -21.54) * mm});
            skPoint(sketch, "E245.visualSharp", {"position": v(78.91, -136.68) * mm});
            skArc(sketch, "E245.filletArc", {"start": v(77.03, -135.27) * mm, "mid": v(78.14, -135.34) * mm, "end": v(78.63, -134.35) * mm});
            skPoint(sketch, "E246.visualSharp", {"position": v(37.32, -125.47) * mm});
            skArc(sketch, "E246.filletArc", {"start": v(34.5, -124.93) * mm, "mid": v(35.54, -124.44) * mm, "end": v(35.44, -123.3) * mm});
            skPoint(sketch, "E247.visualSharp", {"position": v(-37.32, -125.47) * mm});
            skArc(sketch, "E247.filletArc", {"start": v(-35.44, -123.3) * mm, "mid": v(-35.54, -124.44) * mm, "end": v(-34.5, -124.93) * mm});
            skPoint(sketch, "E248.visualSharp", {"position": v(0, -60.83) * mm});
            skArc(sketch, "E248.filletArc", {"start": v(0.94, -63.55) * mm, "mid": v(0, -62.88) * mm, "end": v(-0.94, -63.55) * mm});
            skPoint(sketch, "E249.visualSharp", {"position": v(279.16, -138.08) * mm});
            skArc(sketch, "E249.filletArc", {"start": v(279, -136.35) * mm, "mid": v(279.58, -137.16) * mm, "end": v(280.58, -137.05) * mm});
            skPoint(sketch, "E250.visualSharp", {"position": v(232.68, -30.41) * mm});
            skArc(sketch, "E250.filletArc", {"start": v(235.5, -30.96) * mm, "mid": v(234.46, -31.44) * mm, "end": v(234.56, -32.6) * mm});
            skPoint(sketch, "E251.visualSharp", {"position": v(349.16, -16.84) * mm});
            skArc(sketch, "E251.filletArc", {"start": v(348.98, -18.58) * mm, "mid": v(348.58, -17.66) * mm, "end": v(347.58, -17.56) * mm});
            skPoint(sketch, "E252.visualSharp", {"position": v(-11.09, -19.2) * mm});
            skArc(sketch, "E252.filletArc", {"start": v(-11.37, -21.54) * mm, "mid": v(-11.86, -20.55) * mm, "end": v(-12.97, -20.62) * mm});
            skPoint(sketch, "E253.visualSharp", {"position": v(-78.91, -136.68) * mm});
            skArc(sketch, "E253.filletArc", {"start": v(-78.63, -134.35) * mm, "mid": v(-78.14, -135.34) * mm, "end": v(-77.03, -135.27) * mm});
            skPoint(sketch, "E254.visualSharp", {"position": v(-90, -95.06) * mm});
            skArc(sketch, "E254.filletArc", {"start": v(-90.94, -92.34) * mm, "mid": v(-90, -93) * mm, "end": v(-89.06, -92.34) * mm});
            skPoint(sketch, "E255.visualSharp", {"position": v(-52.68, -30.41) * mm});
            skArc(sketch, "E255.filletArc", {"start": v(-54.56, -32.6) * mm, "mid": v(-54.46, -31.44) * mm, "end": v(-55.5, -30.96) * mm});
            skPoint(sketch, "E256.visualSharp", {"position": v(-127.32, -30.41) * mm});
            skArc(sketch, "E256.filletArc", {"start": v(-124.5, -30.96) * mm, "mid": v(-125.54, -31.44) * mm, "end": v(-125.44, -32.6) * mm});
            skPoint(sketch, "E257.visualSharp", {"position": v(-168.91, -19.2) * mm});
            skArc(sketch, "E257.filletArc", {"start": v(-167.03, -20.62) * mm, "mid": v(-168.14, -20.55) * mm, "end": v(-168.63, -21.54) * mm});
            skPoint(sketch, "E258.visualSharp", {"position": v(-101.09, -136.68) * mm});
            skArc(sketch, "E258.filletArc", {"start": v(-102.97, -135.27) * mm, "mid": v(-101.86, -135.34) * mm, "end": v(-101.37, -134.35) * mm});
            skPoint(sketch, "E259.visualSharp", {"position": v(-217.32, -125.47) * mm});
            skArc(sketch, "E259.filletArc", {"start": v(-215.44, -123.3) * mm, "mid": v(-215.54, -124.44) * mm, "end": v(-214.5, -124.93) * mm});
            skPoint(sketch, "E260.visualSharp", {"position": v(-180, -60.83) * mm});
            skArc(sketch, "E260.filletArc", {"start": v(-179.06, -63.55) * mm, "mid": v(-180, -62.88) * mm, "end": v(-180.94, -63.55) * mm});
            skPoint(sketch, "E261.visualSharp", {"position": v(-142.68, -125.47) * mm});
            skArc(sketch, "E261.filletArc", {"start": v(-145.5, -124.93) * mm, "mid": v(-144.46, -124.44) * mm, "end": v(-144.56, -123.3) * mm});
            skPoint(sketch, "E262.visualSharp", {"position": v(-258.91, -136.68) * mm});
            skArc(sketch, "E262.filletArc", {"start": v(-258.63, -134.35) * mm, "mid": v(-258.14, -135.34) * mm, "end": v(-257.03, -135.27) * mm});
            skPoint(sketch, "E263.visualSharp", {"position": v(-191.09, -19.2) * mm});
            skArc(sketch, "E263.filletArc", {"start": v(-191.37, -21.54) * mm, "mid": v(-191.86, -20.55) * mm, "end": v(-192.97, -20.62) * mm});
            skPoint(sketch, "E264.visualSharp", {"position": v(-232.68, -30.41) * mm});
            skArc(sketch, "E264.filletArc", {"start": v(-234.56, -32.6) * mm, "mid": v(-234.46, -31.44) * mm, "end": v(-235.5, -30.96) * mm});
            skPoint(sketch, "E265.visualSharp", {"position": v(-349.16, -16.84) * mm});
            skArc(sketch, "E265.filletArc", {"start": v(-347.58, -17.56) * mm, "mid": v(-348.58, -17.66) * mm, "end": v(-348.98, -18.58) * mm});
            skPoint(sketch, "E266.visualSharp", {"position": v(-279.16, -138.08) * mm});
            skArc(sketch, "E266.filletArc", {"start": v(-280.58, -137.05) * mm, "mid": v(-279.58, -137.16) * mm, "end": v(-279, -136.35) * mm});
            skPoint(sketch, "E267.visualSharp", {"position": v(-337.82, 0) * mm});
            skArc(sketch, "E267.filletArc", {"start": v(-335.66, 0.92) * mm, "mid": v(-336.28, 0) * mm, "end": v(-335.66, -0.92) * mm});
            skPoint(sketch, "E268.visualSharp", {"position": v(-202.18, 0) * mm});
            skArc(sketch, "E268.filletArc", {"start": v(-204.34, -0.92) * mm, "mid": v(-203.72, 0) * mm, "end": v(-204.34, 0.92) * mm});
            skPoint(sketch, "E269.visualSharp", {"position": v(-157.82, 0) * mm});
            skArc(sketch, "E269.filletArc", {"start": v(-155.66, 0.92) * mm, "mid": v(-156.28, 0) * mm, "end": v(-155.66, -0.92) * mm});
            skPoint(sketch, "E270.visualSharp", {"position": v(-22.18, 0) * mm});
            skArc(sketch, "E270.filletArc", {"start": v(-24.34, -0.92) * mm, "mid": v(-23.72, 0) * mm, "end": v(-24.34, 0.92) * mm});
            skPoint(sketch, "E271.visualSharp", {"position": v(22.18, 0) * mm});
            skArc(sketch, "E271.filletArc", {"start": v(24.34, 0.92) * mm, "mid": v(23.72, 0) * mm, "end": v(24.34, -0.92) * mm});
            skPoint(sketch, "E272.visualSharp", {"position": v(157.82, 0) * mm});
            skArc(sketch, "E272.filletArc", {"start": v(155.66, -0.92) * mm, "mid": v(156.28, 0) * mm, "end": v(155.66, 0.92) * mm});
            skPoint(sketch, "E273.visualSharp", {"position": v(202.18, 0) * mm});
            skArc(sketch, "E273.filletArc", {"start": v(204.34, 0.92) * mm, "mid": v(203.72, 0) * mm, "end": v(204.34, -0.92) * mm});
            skPoint(sketch, "E274.visualSharp", {"position": v(337.82, 0) * mm});
            skArc(sketch, "E274.filletArc", {"start": v(335.66, -0.92) * mm, "mid": v(336.28, 0) * mm, "end": v(335.66, 0.92) * mm});
            skPoint(sketch, "E275.visualSharp", {"position": v(-349.16, 16.84) * mm});
            skArc(sketch, "E275.filletArc", {"start": v(-348.98, 18.58) * mm, "mid": v(-348.58, 17.66) * mm, "end": v(-347.58, 17.56) * mm});
            skPoint(sketch, "E276.visualSharp", {"position": v(-232.68, 30.41) * mm});
            skArc(sketch, "E276.filletArc", {"start": v(-235.5, 30.96) * mm, "mid": v(-234.46, 31.44) * mm, "end": v(-234.56, 32.6) * mm});
            skPoint(sketch, "E277.visualSharp", {"position": v(-279.16, 138.08) * mm});
            skArc(sketch, "E277.filletArc", {"start": v(-279, 136.35) * mm, "mid": v(-279.58, 137.16) * mm, "end": v(-280.58, 137.05) * mm});
            skPoint(sketch, "E278.visualSharp", {"position": v(-258.91, 136.68) * mm});
            skArc(sketch, "E278.filletArc", {"start": v(-257.03, 135.27) * mm, "mid": v(-258.14, 135.34) * mm, "end": v(-258.63, 134.35) * mm});
            skPoint(sketch, "E279.visualSharp", {"position": v(-191.09, 19.2) * mm});
            skArc(sketch, "E279.filletArc", {"start": v(-192.97, 20.62) * mm, "mid": v(-191.86, 20.55) * mm, "end": v(-191.37, 21.54) * mm});
            skPoint(sketch, "E280.visualSharp", {"position": v(-217.32, 125.47) * mm});
            skArc(sketch, "E280.filletArc", {"start": v(-214.5, 124.93) * mm, "mid": v(-215.54, 124.44) * mm, "end": v(-215.44, 123.3) * mm});
            skPoint(sketch, "E281.visualSharp", {"position": v(-142.68, 125.47) * mm});
            skArc(sketch, "E281.filletArc", {"start": v(-144.56, 123.3) * mm, "mid": v(-144.46, 124.44) * mm, "end": v(-145.5, 124.93) * mm});
            skPoint(sketch, "E282.visualSharp", {"position": v(-180, 60.83) * mm});
            skArc(sketch, "E282.filletArc", {"start": v(-180.94, 63.55) * mm, "mid": v(-180, 62.88) * mm, "end": v(-179.06, 63.55) * mm});
            skPoint(sketch, "E283.visualSharp", {"position": v(-168.91, 19.2) * mm});
            skArc(sketch, "E283.filletArc", {"start": v(-168.63, 21.54) * mm, "mid": v(-168.14, 20.55) * mm, "end": v(-167.03, 20.62) * mm});
            skPoint(sketch, "E284.visualSharp", {"position": v(-101.09, 136.68) * mm});
            skArc(sketch, "E284.filletArc", {"start": v(-101.37, 134.35) * mm, "mid": v(-101.86, 135.34) * mm, "end": v(-102.97, 135.27) * mm});
            skPoint(sketch, "E285.visualSharp", {"position": v(-127.32, 30.41) * mm});
            skArc(sketch, "E285.filletArc", {"start": v(-125.44, 32.6) * mm, "mid": v(-125.54, 31.44) * mm, "end": v(-124.5, 30.96) * mm});
            skPoint(sketch, "E286.visualSharp", {"position": v(-90, 95.06) * mm});
            skArc(sketch, "E286.filletArc", {"start": v(-89.06, 92.34) * mm, "mid": v(-90, 93) * mm, "end": v(-90.94, 92.34) * mm});
            skPoint(sketch, "E287.visualSharp", {"position": v(-52.68, 30.41) * mm});
            skArc(sketch, "E287.filletArc", {"start": v(-55.5, 30.96) * mm, "mid": v(-54.46, 31.44) * mm, "end": v(-54.56, 32.6) * mm});
            skPoint(sketch, "E288.visualSharp", {"position": v(-11.09, 19.2) * mm});
            skArc(sketch, "E288.filletArc", {"start": v(-12.97, 20.62) * mm, "mid": v(-11.86, 20.55) * mm, "end": v(-11.37, 21.54) * mm});
            skPoint(sketch, "E289.visualSharp", {"position": v(-78.91, 136.68) * mm});
            skArc(sketch, "E289.filletArc", {"start": v(-77.03, 135.27) * mm, "mid": v(-78.14, 135.34) * mm, "end": v(-78.63, 134.35) * mm});
            skPoint(sketch, "E290.visualSharp", {"position": v(-37.32, 125.47) * mm});
            skArc(sketch, "E290.filletArc", {"start": v(-34.5, 124.93) * mm, "mid": v(-35.54, 124.44) * mm, "end": v(-35.44, 123.3) * mm});
            skPoint(sketch, "E291.visualSharp", {"position": v(37.32, 125.47) * mm});
            skArc(sketch, "E291.filletArc", {"start": v(35.44, 123.3) * mm, "mid": v(35.54, 124.44) * mm, "end": v(34.5, 124.93) * mm});
            skPoint(sketch, "E292.visualSharp", {"position": v(0, 60.83) * mm});
            skArc(sketch, "E292.filletArc", {"start": v(-0.94, 63.55) * mm, "mid": v(0, 62.88) * mm, "end": v(0.94, 63.55) * mm});
            skPoint(sketch, "E293.visualSharp", {"position": v(78.91, 136.68) * mm});
            skArc(sketch, "E293.filletArc", {"start": v(78.63, 134.35) * mm, "mid": v(78.14, 135.34) * mm, "end": v(77.03, 135.27) * mm});
            skPoint(sketch, "E294.visualSharp", {"position": v(11.09, 19.2) * mm});
            skArc(sketch, "E294.filletArc", {"start": v(11.37, 21.54) * mm, "mid": v(11.86, 20.55) * mm, "end": v(12.97, 20.62) * mm});
            skPoint(sketch, "E295.visualSharp", {"position": v(52.68, 30.41) * mm});
            skArc(sketch, "E295.filletArc", {"start": v(54.56, 32.6) * mm, "mid": v(54.46, 31.44) * mm, "end": v(55.5, 30.96) * mm});
            skPoint(sketch, "E296.visualSharp", {"position": v(127.32, 30.41) * mm});
            skArc(sketch, "E296.filletArc", {"start": v(124.5, 30.96) * mm, "mid": v(125.54, 31.44) * mm, "end": v(125.44, 32.6) * mm});
            skPoint(sketch, "E297.visualSharp", {"position": v(90, 95.06) * mm});
            skArc(sketch, "E297.filletArc", {"start": v(90.94, 92.34) * mm, "mid": v(90, 93) * mm, "end": v(89.06, 92.34) * mm});
            skPoint(sketch, "E298.visualSharp", {"position": v(101.09, 136.68) * mm});
            skArc(sketch, "E298.filletArc", {"start": v(102.97, 135.27) * mm, "mid": v(101.86, 135.34) * mm, "end": v(101.37, 134.35) * mm});
            skPoint(sketch, "E299.visualSharp", {"position": v(168.91, 19.2) * mm});
            skArc(sketch, "E299.filletArc", {"start": v(167.03, 20.62) * mm, "mid": v(168.14, 20.55) * mm, "end": v(168.63, 21.54) * mm});
            skPoint(sketch, "E300.visualSharp", {"position": v(180, 60.83) * mm});
            skArc(sketch, "E300.filletArc", {"start": v(179.06, 63.55) * mm, "mid": v(180, 62.88) * mm, "end": v(180.94, 63.55) * mm});
            skPoint(sketch, "E301.visualSharp", {"position": v(142.68, 125.47) * mm});
            skArc(sketch, "E301.filletArc", {"start": v(145.5, 124.93) * mm, "mid": v(144.46, 124.44) * mm, "end": v(144.56, 123.3) * mm});
            skPoint(sketch, "E302.visualSharp", {"position": v(217.32, 125.47) * mm});
            skArc(sketch, "E302.filletArc", {"start": v(215.44, 123.3) * mm, "mid": v(215.54, 124.44) * mm, "end": v(214.5, 124.93) * mm});
            skPoint(sketch, "E303.visualSharp", {"position": v(191.09, 19.2) * mm});
            skArc(sketch, "E303.filletArc", {"start": v(191.37, 21.54) * mm, "mid": v(191.86, 20.55) * mm, "end": v(192.97, 20.62) * mm});
            skPoint(sketch, "E304.visualSharp", {"position": v(258.91, 136.68) * mm});
            skArc(sketch, "E304.filletArc", {"start": v(258.63, 134.35) * mm, "mid": v(258.14, 135.34) * mm, "end": v(257.03, 135.27) * mm});
            skPoint(sketch, "E305.visualSharp", {"position": v(232.68, 30.41) * mm});
            skArc(sketch, "E305.filletArc", {"start": v(234.56, 32.6) * mm, "mid": v(234.46, 31.44) * mm, "end": v(235.5, 30.96) * mm});
            skPoint(sketch, "E306.visualSharp", {"position": v(279.16, 138.08) * mm});
            skArc(sketch, "E306.filletArc", {"start": v(280.58, 137.05) * mm, "mid": v(279.58, 137.16) * mm, "end": v(279, 136.35) * mm});
            skPoint(sketch, "E307.visualSharp", {"position": v(349.16, 16.84) * mm});
            skArc(sketch, "E307.filletArc", {"start": v(347.58, 17.56) * mm, "mid": v(348.58, 17.66) * mm, "end": v(348.98, 18.58) * mm});
            skPoint(sketch, "E308.visualSharp", {"position": v(-247.82, 155.88) * mm});
            skArc(sketch, "E308.filletArc", {"start": v(-245.66, 156.8) * mm, "mid": v(-246.28, 155.88) * mm, "end": v(-245.66, 154.96) * mm});
            skPoint(sketch, "E309.visualSharp", {"position": v(-112.18, 155.88) * mm});
            skArc(sketch, "E309.filletArc", {"start": v(-114.34, 154.96) * mm, "mid": v(-113.72, 155.88) * mm, "end": v(-114.34, 156.8) * mm});
            skPoint(sketch, "E310.visualSharp", {"position": v(-67.82, 155.88) * mm});
            skArc(sketch, "E310.filletArc", {"start": v(-65.66, 156.8) * mm, "mid": v(-66.28, 155.88) * mm, "end": v(-65.66, 154.96) * mm});
            skPoint(sketch, "E311.visualSharp", {"position": v(67.82, 155.88) * mm});
            skArc(sketch, "E311.filletArc", {"start": v(65.66, 154.96) * mm, "mid": v(66.28, 155.88) * mm, "end": v(65.66, 156.8) * mm});
            skPoint(sketch, "E312.visualSharp", {"position": v(112.18, 155.88) * mm});
            skArc(sketch, "E312.filletArc", {"start": v(114.34, 156.8) * mm, "mid": v(113.72, 155.88) * mm, "end": v(114.34, 154.96) * mm});
            skPoint(sketch, "E313.visualSharp", {"position": v(247.82, 155.88) * mm});
            skArc(sketch, "E313.filletArc", {"start": v(245.66, 154.96) * mm, "mid": v(246.28, 155.88) * mm, "end": v(245.66, 156.8) * mm});
            skPoint(sketch, "E314.visualSharp", {"position": v(142.68, 186.3) * mm});
            skArc(sketch, "E314.filletArc", {"start": v(144.56, 188.47) * mm, "mid": v(144.46, 187.33) * mm, "end": v(145.5, 186.84) * mm});
            skPoint(sketch, "E315.visualSharp", {"position": v(189.16, 293.97) * mm});
            skArc(sketch, "E315.filletArc", {"start": v(190.58, 292.94) * mm, "mid": v(189.58, 293.05) * mm, "end": v(189, 292.24) * mm});
            skPoint(sketch, "E316.visualSharp", {"position": v(259.16, 172.72) * mm});
            skArc(sketch, "E316.filletArc", {"start": v(257.58, 173.44) * mm, "mid": v(258.58, 173.54) * mm, "end": v(258.98, 174.46) * mm});
            skPoint(sketch, "E317.visualSharp", {"position": v(-259.16, 172.72) * mm});
            skArc(sketch, "E317.filletArc", {"start": v(-258.98, 174.46) * mm, "mid": v(-258.58, 173.54) * mm, "end": v(-257.58, 173.44) * mm});
            skPoint(sketch, "E318.visualSharp", {"position": v(-142.68, 186.3) * mm});
            skArc(sketch, "E318.filletArc", {"start": v(-145.5, 186.84) * mm, "mid": v(-144.46, 187.33) * mm, "end": v(-144.56, 188.47) * mm});
            skPoint(sketch, "E319.visualSharp", {"position": v(-189.16, 293.97) * mm});
            skArc(sketch, "E319.filletArc", {"start": v(-189, 292.24) * mm, "mid": v(-189.58, 293.05) * mm, "end": v(-190.58, 292.94) * mm});
            skPoint(sketch, "E320.visualSharp", {"position": v(-168.91, 292.56) * mm});
            skArc(sketch, "E320.filletArc", {"start": v(-167.03, 291.15) * mm, "mid": v(-168.14, 291.22) * mm, "end": v(-168.63, 290.23) * mm});
            skPoint(sketch, "E321.visualSharp", {"position": v(-101.09, 175.1) * mm});
            skArc(sketch, "E321.filletArc", {"start": v(-102.97, 176.5) * mm, "mid": v(-101.86, 176.43) * mm, "end": v(-101.37, 177.42) * mm});
            skPoint(sketch, "E322.visualSharp", {"position": v(101.09, 175.1) * mm});
            skArc(sketch, "E322.filletArc", {"start": v(101.37, 177.42) * mm, "mid": v(101.86, 176.43) * mm, "end": v(102.97, 176.5) * mm});
            skPoint(sketch, "E323.visualSharp", {"position": v(168.91, 292.56) * mm});
            skArc(sketch, "E323.filletArc", {"start": v(168.63, 290.23) * mm, "mid": v(168.14, 291.22) * mm, "end": v(167.03, 291.15) * mm});
            skPoint(sketch, "E324.visualSharp", {"position": v(-37.32, 186.3) * mm});
            skArc(sketch, "E324.filletArc", {"start": v(-35.44, 188.47) * mm, "mid": v(-35.54, 187.33) * mm, "end": v(-34.5, 186.84) * mm});
            skPoint(sketch, "E325.visualSharp", {"position": v(0, 250.94) * mm});
            skArc(sketch, "E325.filletArc", {"start": v(0.94, 248.22) * mm, "mid": v(0, 248.89) * mm, "end": v(-0.94, 248.22) * mm});
            skPoint(sketch, "E326.visualSharp", {"position": v(37.32, 186.3) * mm});
            skArc(sketch, "E326.filletArc", {"start": v(34.5, 186.84) * mm, "mid": v(35.54, 187.33) * mm, "end": v(35.44, 188.47) * mm});
            skPoint(sketch, "E327.visualSharp", {"position": v(-11.09, 292.56) * mm});
            skArc(sketch, "E327.filletArc", {"start": v(-11.37, 290.23) * mm, "mid": v(-11.86, 291.22) * mm, "end": v(-12.97, 291.15) * mm});
            skPoint(sketch, "E328.visualSharp", {"position": v(-78.91, 175.1) * mm});
            skArc(sketch, "E328.filletArc", {"start": v(-78.63, 177.42) * mm, "mid": v(-78.14, 176.43) * mm, "end": v(-77.03, 176.5) * mm});
            skPoint(sketch, "E329.visualSharp", {"position": v(11.09, 292.56) * mm});
            skArc(sketch, "E329.filletArc", {"start": v(12.97, 291.15) * mm, "mid": v(11.86, 291.22) * mm, "end": v(11.37, 290.23) * mm});
            skPoint(sketch, "E330.visualSharp", {"position": v(78.91, 175.1) * mm});
            skArc(sketch, "E330.filletArc", {"start": v(77.03, 176.5) * mm, "mid": v(78.14, 176.43) * mm, "end": v(78.63, 177.42) * mm});
            skPoint(sketch, "E331.visualSharp", {"position": v(90, 216.71) * mm});
            skArc(sketch, "E331.filletArc", {"start": v(89.06, 219.43) * mm, "mid": v(90, 218.77) * mm, "end": v(90.94, 219.43) * mm});
            skPoint(sketch, "E332.visualSharp", {"position": v(20, 310.8) * mm});
            skArc(sketch, "E332.filletArc", {"start": v(21.6, 311.52) * mm, "mid": v(21, 310.7) * mm, "end": v(21.41, 309.8) * mm});
            skPoint(sketch, "E333.visualSharp", {"position": v(160, 310.8) * mm});
            skArc(sketch, "E333.filletArc", {"start": v(158.59, 309.8) * mm, "mid": v(159, 310.7) * mm, "end": v(158.4, 311.52) * mm});
            skPoint(sketch, "E334.visualSharp", {"position": v(-160, 310.8) * mm});
            skArc(sketch, "E334.filletArc", {"start": v(-158.4, 311.52) * mm, "mid": v(-159, 310.7) * mm, "end": v(-158.59, 309.8) * mm});
            skPoint(sketch, "E335.visualSharp", {"position": v(-90, 216.71) * mm});
            skArc(sketch, "E335.filletArc", {"start": v(-90.94, 219.43) * mm, "mid": v(-90, 218.77) * mm, "end": v(-89.06, 219.43) * mm});
            skPoint(sketch, "E336.visualSharp", {"position": v(-20, 310.8) * mm});
            skArc(sketch, "E336.filletArc", {"start": v(-21.41, 309.8) * mm, "mid": v(-21, 310.7) * mm, "end": v(-21.6, 311.52) * mm});
            skSolve(sketch);
        }
        {
            var Q0;
            Q0=makeQuery(id+"F0.imprint","IMPRINT",FACE,{"disambiguationData":[TD([[makeQuery(id+"F0.imprint","IMPRINT",EDGE,{"derivedFrom":sQuery(id+"F0.wireOp",EDGE,"E0")}),-1.0]])]});
            extrude(context, id + "F1", {"entities" : qUnion([Q0]), "depth" : 3 * mm});
        }
        {
            var Q0;
            Q0=makeQuery(id+"F1.opExtrude","CAP_FACE",FACE,{"disambiguationData":[OSD([sQuery(id+"F0.wireOp",EDGE,"E0"),sQuery(id+"F0.wireOp",EDGE,"E1"),sQuery(id+"F0.wireOp",EDGE,"E2"),sQuery(id+"F0.wireOp",EDGE,"E3"),sQuery(id+"F0.wireOp",EDGE,"E4"),sQuery(id+"F0.wireOp",EDGE,"E5"),sQuery(id+"F0.wireOp",EDGE,"E6"),sQuery(id+"F0.wireOp",EDGE,"E7"),sQuery(id+"F0.wireOp",EDGE,"E8"),sQuery(id+"F0.wireOp",EDGE,"E9"),sQuery(id+"F0.wireOp",EDGE,"E10"),sQuery(id+"F0.wireOp",EDGE,"E11"),sQuery(id+"F0.wireOp",EDGE,"E12"),sQuery(id+"F0.wireOp",EDGE,"E13"),sQuery(id+"F0.wireOp",EDGE,"E14"),sQuery(id+"F0.wireOp",EDGE,"E15"),sQuery(id+"F0.wireOp",EDGE,"E16.trimOffspring"),sQuery(id+"F0.wireOp",EDGE,"E17.trimOffspring"),sQuery(id+"F0.wireOp",EDGE,"E18.trimOffspring"),sQuery(id+"F0.wireOp",EDGE,"E19.trimOffspring"),sQuery(id+"F0.wireOp",EDGE,"E20.trimOffspring"),sQuery(id+"F0.wireOp",EDGE,"E21.trimOffspring"),sQuery(id+"F0.wireOp",EDGE,"E22.trimOffspring"),sQuery(id+"F0.wireOp",EDGE,"E23.trimOffspring"),sQuery(id+"F0.wireOp",EDGE,"E24.trimOffspring"),sQuery(id+"F0.wireOp",EDGE,"E25.trimOffspring"),sQuery(id+"F0.wireOp",EDGE,"E26.trimOffspring"),sQuery(id+"F0.wireOp",EDGE,"E27.trimOffspring"),sQuery(id+"F0.wireOp",EDGE,"E28.trimOffspring"),sQuery(id+"F0.wireOp",EDGE,"E29.trimOffspring"),sQuery(id+"F0.wireOp",EDGE,"E30.trimOffspring"),sQuery(id+"F0.wireOp",EDGE,"E31.trimOffspring"),sQuery(id+"F0.wireOp",EDGE,"E32.trimOffspring"),sQuery(id+"F0.wireOp",EDGE,"E33.trimOffspring"),sQuery(id+"F0.wireOp",EDGE,"E34.trimOffspring"),sQuery(id+"F0.wireOp",EDGE,"E35.trimOffspring"),sQuery(id+"F0.wireOp",EDGE,"E36.trimOffspring"),sQuery(id+"F0.wireOp",EDGE,"E37.trimOffspring"),sQuery(id+"F0.wireOp",EDGE,"E38.trimOffspring"),sQuery(id+"F0.wireOp",EDGE,"E39.trimOffspring"),sQuery(id+"F0.wireOp",EDGE,"E40.trimOffspring"),sQuery(id+"F0.wireOp",EDGE,"E41.trimOffspring"),sQuery(id+"F0.wireOp",EDGE,"E42.trimOffspring"),sQuery(id+"F0.wireOp",EDGE,"E43.trimOffspring"),sQuery(id+"F0.wireOp",EDGE,"E44.trimOffspring"),sQuery(id+"F0.wireOp",EDGE,"E45.trimOffspring"),sQuery(id+"F0.wireOp",EDGE,"E46.trimOffspring"),sQuery(id+"F0.wireOp",EDGE,"E47.trimOffspring"),sQuery(id+"F0.wireOp",EDGE,"E48.trimOffspring"),sQuery(id+"F0.wireOp",EDGE,"E49.trimOffspring"),sQuery(id+"F0.wireOp",EDGE,"E50.trimOffspring"),sQuery(id+"F0.wireOp",EDGE,"E51.trimOffspring"),sQuery(id+"F0.wireOp",EDGE,"E52.trimOffspring"),sQuery(id+"F0.wireOp",EDGE,"E53.trimOffspring"),sQuery(id+"F0.wireOp",EDGE,"E54.trimOffspring"),sQuery(id+"F0.wireOp",EDGE,"E55.trimOffspring"),sQuery(id+"F0.wireOp",EDGE,"E56.trimOffspring"),sQuery(id+"F0.wireOp",EDGE,"E57.trimOffspring"),sQuery(id+"F0.wireOp",EDGE,"E58.trimOffspring"),sQuery(id+"F0.wireOp",EDGE,"E59.trimOffspring"),sQuery(id+"F0.wireOp",EDGE,"E60.trimOffspring"),sQuery(id+"F0.wireOp",EDGE,"E61.trimOffspring"),sQuery(id+"F0.wireOp",EDGE,"E62.trimOffspring"),sQuery(id+"F0.wireOp",EDGE,"E63.trimOffspring"),sQuery(id+"F0.wireOp",EDGE,"E64.trimOffspring"),sQuery(id+"F0.wireOp",EDGE,"E65.trimOffspring"),sQuery(id+"F0.wireOp",EDGE,"E66.trimOffspring"),sQuery(id+"F0.wireOp",EDGE,"E67.trimOffspring"),sQuery(id+"F0.wireOp",EDGE,"E68.trimOffspring"),sQuery(id+"F0.wireOp",EDGE,"E69.trimOffspring"),sQuery(id+"F0.wireOp",EDGE,"E70.trimOffspring"),sQuery(id+"F0.wireOp",EDGE,"E71.trimOffspring"),sQuery(id+"F0.wireOp",EDGE,"E72.trimOffspring"),sQuery(id+"F0.wireOp",EDGE,"E73.trimOffspring"),sQuery(id+"F0.wireOp",EDGE,"E74.trimOffspring"),sQuery(id+"F0.wireOp",EDGE,"E75.trimOffspring"),sQuery(id+"F0.wireOp",EDGE,"E76.trimOffspring"),sQuery(id+"F0.wireOp",EDGE,"E77.trimOffspring"),sQuery(id+"F0.wireOp",EDGE,"E78.trimOffspring"),sQuery(id+"F0.wireOp",EDGE,"E79.trimOffspring"),sQuery(id+"F0.wireOp",EDGE,"E80.trimOffspring"),sQuery(id+"F0.wireOp",EDGE,"E81.trimOffspring"),sQuery(id+"F0.wireOp",EDGE,"E82.trimOffspring"),sQuery(id+"F0.wireOp",EDGE,"E83.trimOffspring"),sQuery(id+"F0.wireOp",EDGE,"E84.trimOffspring"),sQuery(id+"F0.wireOp",EDGE,"E85.trimOffspring"),sQuery(id+"F0.wireOp",EDGE,"E86.trimOffspring"),sQuery(id+"F0.wireOp",EDGE,"E87.trimOffspring"),sQuery(id+"F0.wireOp",EDGE,"E88.trimOffspring"),sQuery(id+"F0.wireOp",EDGE,"E89.trimOffspring"),sQuery(id+"F0.wireOp",EDGE,"E90.trimOffspring"),sQuery(id+"F0.wireOp",EDGE,"E91.trimOffspring"),sQuery(id+"F0.wireOp",EDGE,"E92.trimOffspring"),sQuery(id+"F0.wireOp",EDGE,"E93.trimOffspring"),sQuery(id+"F0.wireOp",EDGE,"E94.trimOffspring"),sQuery(id+"F0.wireOp",EDGE,"E95.trimOffspring"),sQuery(id+"F0.wireOp",EDGE,"E96.trimOffspring"),sQuery(id+"F0.wireOp",EDGE,"E97.trimOffspring"),sQuery(id+"F0.wireOp",EDGE,"E98.trimOffspring"),sQuery(id+"F0.wireOp",EDGE,"E99.trimOffspring"),sQuery(id+"F0.wireOp",EDGE,"E100.trimOffspring"),sQuery(id+"F0.wireOp",EDGE,"E101.trimOffspring"),sQuery(id+"F0.wireOp",EDGE,"E102.trimOffspring"),sQuery(id+"F0.wireOp",EDGE,"E103.trimOffspring"),sQuery(id+"F0.wireOp",EDGE,"E104.trimOffspring"),sQuery(id+"F0.wireOp",EDGE,"E105.trimOffspring"),sQuery(id+"F0.wireOp",EDGE,"E106.trimOffspring"),sQuery(id+"F0.wireOp",EDGE,"E107.trimOffspring"),sQuery(id+"F0.wireOp",EDGE,"E108.trimOffspring"),sQuery(id+"F0.wireOp",EDGE,"E109.trimOffspring"),sQuery(id+"F0.wireOp",EDGE,"E110.trimOffspring"),sQuery(id+"F0.wireOp",EDGE,"E111.trimOffspring"),sQuery(id+"F0.wireOp",EDGE,"E112.trimOffspring"),sQuery(id+"F0.wireOp",EDGE,"E113.trimOffspring"),sQuery(id+"F0.wireOp",EDGE,"E114.trimOffspring"),sQuery(id+"F0.wireOp",EDGE,"E115.trimOffspring"),sQuery(id+"F0.wireOp",EDGE,"E116.trimOffspring"),sQuery(id+"F0.wireOp",EDGE,"E117.trimOffspring"),sQuery(id+"F0.wireOp",EDGE,"E118.trimOffspring"),sQuery(id+"F0.wireOp",EDGE,"E119.trimOffspring"),sQuery(id+"F0.wireOp",EDGE,"E120.trimOffspring"),sQuery(id+"F0.wireOp",EDGE,"E121.trimOffspring"),sQuery(id+"F0.wireOp",EDGE,"E122.trimOffspring"),sQuery(id+"F0.wireOp",EDGE,"E123.trimOffspring"),sQuery(id+"F0.wireOp",EDGE,"E124.trimOffspring"),sQuery(id+"F0.wireOp",EDGE,"E125.trimOffspring"),sQuery(id+"F0.wireOp",EDGE,"E126.trimOffspring"),sQuery(id+"F0.wireOp",EDGE,"E127.trimOffspring"),sQuery(id+"F0.wireOp",EDGE,"E128.trimOffspring"),sQuery(id+"F0.wireOp",EDGE,"E129.trimOffspring"),sQuery(id+"F0.wireOp",EDGE,"E130.trimOffspring"),sQuery(id+"F0.wireOp",EDGE,"E131.trimOffspring"),sQuery(id+"F0.wireOp",EDGE,"E132.trimOffspring"),sQuery(id+"F0.wireOp",EDGE,"E133.trimOffspring"),sQuery(id+"F0.wireOp",EDGE,"E134.trimOffspring"),sQuery(id+"F0.wireOp",EDGE,"E135.trimOffspring"),sQuery(id+"F0.wireOp",EDGE,"E136.trimOffspring"),sQuery(id+"F0.wireOp",EDGE,"E137.trimOffspring"),sQuery(id+"F0.wireOp",EDGE,"E138.trimOffspring"),sQuery(id+"F0.wireOp",EDGE,"E139.trimOffspring"),sQuery(id+"F0.wireOp",EDGE,"E140.trimOffspring"),sQuery(id+"F0.wireOp",EDGE,"E141.trimOffspring"),sQuery(id+"F0.wireOp",EDGE,"E142.trimOffspring"),sQuery(id+"F0.wireOp",EDGE,"E143.trimOffspring"),sQuery(id+"F0.wireOp",EDGE,"E144.trimOffspring"),sQuery(id+"F0.wireOp",EDGE,"E145.trimOffspring"),sQuery(id+"F0.wireOp",EDGE,"E146.trimOffspring"),sQuery(id+"F0.wireOp",EDGE,"E147.trimOffspring"),sQuery(id+"F0.wireOp",EDGE,"E148.trimOffspring"),sQuery(id+"F0.wireOp",EDGE,"E149.trimOffspring"),sQuery(id+"F0.wireOp",EDGE,"E150.trimOffspring"),sQuery(id+"F0.wireOp",EDGE,"E151.trimOffspring"),sQuery(id+"F0.wireOp",EDGE,"E152.trimOffspring"),sQuery(id+"F0.wireOp",EDGE,"E153.trimOffspring"),sQuery(id+"F0.wireOp",EDGE,"E154.trimOffspring"),sQuery(id+"F0.wireOp",EDGE,"E155.trimOffspring"),sQuery(id+"F0.wireOp",EDGE,"E156.trimOffspring"),sQuery(id+"F0.wireOp",EDGE,"E157.trimOffspring"),sQuery(id+"F0.wireOp",EDGE,"E158.trimOffspring"),sQuery(id+"F0.wireOp",EDGE,"E159.trimOffspring"),sQuery(id+"F0.wireOp",EDGE,"E160.trimOffspring"),sQuery(id+"F0.wireOp",EDGE,"E161.trimOffspring"),sQuery(id+"F0.wireOp",EDGE,"E162.trimOffspring"),sQuery(id+"F0.wireOp",EDGE,"E163.trimOffspring"),sQuery(id+"F0.wireOp",EDGE,"E164.trimOffspring"),sQuery(id+"F0.wireOp",EDGE,"E165.trimOffspring"),sQuery(id+"F0.wireOp",EDGE,"E166.trimOffspring"),sQuery(id+"F0.wireOp",EDGE,"E167.trimOffspring"),sQuery(id+"F0.wireOp",EDGE,"E168.trimOffspring"),sQuery(id+"F0.wireOp",EDGE,"E169.filletArc"),sQuery(id+"F0.wireOp",EDGE,"E170.filletArc"),sQuery(id+"F0.wireOp",EDGE,"E171.filletArc"),sQuery(id+"F0.wireOp",EDGE,"E172.filletArc"),sQuery(id+"F0.wireOp",EDGE,"E173.filletArc"),sQuery(id+"F0.wireOp",EDGE,"E174.filletArc"),sQuery(id+"F0.wireOp",EDGE,"E175.filletArc"),sQuery(id+"F0.wireOp",EDGE,"E176.filletArc"),sQuery(id+"F0.wireOp",EDGE,"E177.filletArc"),sQuery(id+"F0.wireOp",EDGE,"E178.filletArc"),sQuery(id+"F0.wireOp",EDGE,"E179.filletArc"),sQuery(id+"F0.wireOp",EDGE,"E180.filletArc"),sQuery(id+"F0.wireOp",EDGE,"E181.filletArc"),sQuery(id+"F0.wireOp",EDGE,"E182.filletArc"),sQuery(id+"F0.wireOp",EDGE,"E183.filletArc"),sQuery(id+"F0.wireOp",EDGE,"E184.filletArc"),sQuery(id+"F0.wireOp",EDGE,"E185.filletArc"),sQuery(id+"F0.wireOp",EDGE,"E186.filletArc"),sQuery(id+"F0.wireOp",EDGE,"E187.filletArc"),sQuery(id+"F0.wireOp",EDGE,"E188.filletArc"),sQuery(id+"F0.wireOp",EDGE,"E189.filletArc"),sQuery(id+"F0.wireOp",EDGE,"E190.filletArc"),sQuery(id+"F0.wireOp",EDGE,"E191.filletArc"),sQuery(id+"F0.wireOp",EDGE,"E192.filletArc"),sQuery(id+"F0.wireOp",EDGE,"E193.filletArc"),sQuery(id+"F0.wireOp",EDGE,"E194.filletArc"),sQuery(id+"F0.wireOp",EDGE,"E195.filletArc"),sQuery(id+"F0.wireOp",EDGE,"E196.filletArc"),sQuery(id+"F0.wireOp",EDGE,"E197.filletArc"),sQuery(id+"F0.wireOp",EDGE,"E198.filletArc"),sQuery(id+"F0.wireOp",EDGE,"E199.filletArc"),sQuery(id+"F0.wireOp",EDGE,"E200.filletArc"),sQuery(id+"F0.wireOp",EDGE,"E201.filletArc"),sQuery(id+"F0.wireOp",EDGE,"E202.filletArc"),sQuery(id+"F0.wireOp",EDGE,"E203.filletArc"),sQuery(id+"F0.wireOp",EDGE,"E204.filletArc"),sQuery(id+"F0.wireOp",EDGE,"E205.filletArc"),sQuery(id+"F0.wireOp",EDGE,"E206.filletArc"),sQuery(id+"F0.wireOp",EDGE,"E207.filletArc"),sQuery(id+"F0.wireOp",EDGE,"E208.filletArc"),sQuery(id+"F0.wireOp",EDGE,"E209.filletArc"),sQuery(id+"F0.wireOp",EDGE,"E210.filletArc"),sQuery(id+"F0.wireOp",EDGE,"E211.filletArc"),sQuery(id+"F0.wireOp",EDGE,"E212.filletArc"),sQuery(id+"F0.wireOp",EDGE,"E213.filletArc"),sQuery(id+"F0.wireOp",EDGE,"E214.filletArc"),sQuery(id+"F0.wireOp",EDGE,"E215.filletArc"),sQuery(id+"F0.wireOp",EDGE,"E216.filletArc"),sQuery(id+"F0.wireOp",EDGE,"E217.filletArc"),sQuery(id+"F0.wireOp",EDGE,"E218.filletArc"),sQuery(id+"F0.wireOp",EDGE,"E219.filletArc"),sQuery(id+"F0.wireOp",EDGE,"E220.filletArc"),sQuery(id+"F0.wireOp",EDGE,"E221.filletArc"),sQuery(id+"F0.wireOp",EDGE,"E222.filletArc"),sQuery(id+"F0.wireOp",EDGE,"E223.filletArc"),sQuery(id+"F0.wireOp",EDGE,"E224.filletArc"),sQuery(id+"F0.wireOp",EDGE,"E225.filletArc"),sQuery(id+"F0.wireOp",EDGE,"E226.filletArc"),sQuery(id+"F0.wireOp",EDGE,"E227.filletArc"),sQuery(id+"F0.wireOp",EDGE,"E228.filletArc"),sQuery(id+"F0.wireOp",EDGE,"E229.filletArc"),sQuery(id+"F0.wireOp",EDGE,"E230.filletArc"),sQuery(id+"F0.wireOp",EDGE,"E231.filletArc"),sQuery(id+"F0.wireOp",EDGE,"E232.filletArc"),sQuery(id+"F0.wireOp",EDGE,"E233.filletArc"),sQuery(id+"F0.wireOp",EDGE,"E234.filletArc"),sQuery(id+"F0.wireOp",EDGE,"E235.filletArc"),sQuery(id+"F0.wireOp",EDGE,"E236.filletArc"),sQuery(id+"F0.wireOp",EDGE,"E237.filletArc"),sQuery(id+"F0.wireOp",EDGE,"E238.filletArc"),sQuery(id+"F0.wireOp",EDGE,"E239.filletArc"),sQuery(id+"F0.wireOp",EDGE,"E240.filletArc"),sQuery(id+"F0.wireOp",EDGE,"E241.filletArc"),sQuery(id+"F0.wireOp",EDGE,"E242.filletArc"),sQuery(id+"F0.wireOp",EDGE,"E243.filletArc"),sQuery(id+"F0.wireOp",EDGE,"E244.filletArc"),sQuery(id+"F0.wireOp",EDGE,"E245.filletArc"),sQuery(id+"F0.wireOp",EDGE,"E246.filletArc"),sQuery(id+"F0.wireOp",EDGE,"E247.filletArc"),sQuery(id+"F0.wireOp",EDGE,"E248.filletArc"),sQuery(id+"F0.wireOp",EDGE,"E249.filletArc"),sQuery(id+"F0.wireOp",EDGE,"E250.filletArc"),sQuery(id+"F0.wireOp",EDGE,"E251.filletArc"),sQuery(id+"F0.wireOp",EDGE,"E252.filletArc"),sQuery(id+"F0.wireOp",EDGE,"E253.filletArc"),sQuery(id+"F0.wireOp",EDGE,"E254.filletArc"),sQuery(id+"F0.wireOp",EDGE,"E255.filletArc"),sQuery(id+"F0.wireOp",EDGE,"E256.filletArc"),sQuery(id+"F0.wireOp",EDGE,"E257.filletArc"),sQuery(id+"F0.wireOp",EDGE,"E258.filletArc"),sQuery(id+"F0.wireOp",EDGE,"E259.filletArc"),sQuery(id+"F0.wireOp",EDGE,"E260.filletArc"),sQuery(id+"F0.wireOp",EDGE,"E261.filletArc"),sQuery(id+"F0.wireOp",EDGE,"E262.filletArc"),sQuery(id+"F0.wireOp",EDGE,"E263.filletArc"),sQuery(id+"F0.wireOp",EDGE,"E264.filletArc"),sQuery(id+"F0.wireOp",EDGE,"E265.filletArc"),sQuery(id+"F0.wireOp",EDGE,"E266.filletArc"),sQuery(id+"F0.wireOp",EDGE,"E267.filletArc"),sQuery(id+"F0.wireOp",EDGE,"E268.filletArc"),sQuery(id+"F0.wireOp",EDGE,"E269.filletArc"),sQuery(id+"F0.wireOp",EDGE,"E270.filletArc"),sQuery(id+"F0.wireOp",EDGE,"E271.filletArc"),sQuery(id+"F0.wireOp",EDGE,"E272.filletArc"),sQuery(id+"F0.wireOp",EDGE,"E273.filletArc"),sQuery(id+"F0.wireOp",EDGE,"E274.filletArc"),sQuery(id+"F0.wireOp",EDGE,"E275.filletArc"),sQuery(id+"F0.wireOp",EDGE,"E276.filletArc"),sQuery(id+"F0.wireOp",EDGE,"E277.filletArc"),sQuery(id+"F0.wireOp",EDGE,"E278.filletArc"),sQuery(id+"F0.wireOp",EDGE,"E279.filletArc"),sQuery(id+"F0.wireOp",EDGE,"E280.filletArc"),sQuery(id+"F0.wireOp",EDGE,"E281.filletArc"),sQuery(id+"F0.wireOp",EDGE,"E282.filletArc"),sQuery(id+"F0.wireOp",EDGE,"E283.filletArc"),sQuery(id+"F0.wireOp",EDGE,"E284.filletArc"),sQuery(id+"F0.wireOp",EDGE,"E285.filletArc"),sQuery(id+"F0.wireOp",EDGE,"E286.filletArc"),sQuery(id+"F0.wireOp",EDGE,"E287.filletArc"),sQuery(id+"F0.wireOp",EDGE,"E288.filletArc"),sQuery(id+"F0.wireOp",EDGE,"E289.filletArc"),sQuery(id+"F0.wireOp",EDGE,"E290.filletArc"),sQuery(id+"F0.wireOp",EDGE,"E291.filletArc"),sQuery(id+"F0.wireOp",EDGE,"E292.filletArc"),sQuery(id+"F0.wireOp",EDGE,"E293.filletArc"),sQuery(id+"F0.wireOp",EDGE,"E294.filletArc"),sQuery(id+"F0.wireOp",EDGE,"E295.filletArc"),sQuery(id+"F0.wireOp",EDGE,"E296.filletArc"),sQuery(id+"F0.wireOp",EDGE,"E297.filletArc"),sQuery(id+"F0.wireOp",EDGE,"E298.filletArc"),sQuery(id+"F0.wireOp",EDGE,"E299.filletArc"),sQuery(id+"F0.wireOp",EDGE,"E300.filletArc"),sQuery(id+"F0.wireOp",EDGE,"E301.filletArc"),sQuery(id+"F0.wireOp",EDGE,"E302.filletArc"),sQuery(id+"F0.wireOp",EDGE,"E303.filletArc"),sQuery(id+"F0.wireOp",EDGE,"E304.filletArc"),sQuery(id+"F0.wireOp",EDGE,"E305.filletArc"),sQuery(id+"F0.wireOp",EDGE,"E306.filletArc"),sQuery(id+"F0.wireOp",EDGE,"E307.filletArc"),sQuery(id+"F0.wireOp",EDGE,"E308.filletArc"),sQuery(id+"F0.wireOp",EDGE,"E309.filletArc"),sQuery(id+"F0.wireOp",EDGE,"E310.filletArc"),sQuery(id+"F0.wireOp",EDGE,"E311.filletArc"),sQuery(id+"F0.wireOp",EDGE,"E312.filletArc"),sQuery(id+"F0.wireOp",EDGE,"E313.filletArc"),sQuery(id+"F0.wireOp",EDGE,"E314.filletArc"),sQuery(id+"F0.wireOp",EDGE,"E315.filletArc"),sQuery(id+"F0.wireOp",EDGE,"E316.filletArc"),sQuery(id+"F0.wireOp",EDGE,"E317.filletArc"),sQuery(id+"F0.wireOp",EDGE,"E318.filletArc"),sQuery(id+"F0.wireOp",EDGE,"E319.filletArc"),sQuery(id+"F0.wireOp",EDGE,"E320.filletArc"),sQuery(id+"F0.wireOp",EDGE,"E321.filletArc"),sQuery(id+"F0.wireOp",EDGE,"E322.filletArc"),sQuery(id+"F0.wireOp",EDGE,"E323.filletArc"),sQuery(id+"F0.wireOp",EDGE,"E324.filletArc"),sQuery(id+"F0.wireOp",EDGE,"E325.filletArc"),sQuery(id+"F0.wireOp",EDGE,"E326.filletArc"),sQuery(id+"F0.wireOp",EDGE,"E327.filletArc"),sQuery(id+"F0.wireOp",EDGE,"E328.filletArc"),sQuery(id+"F0.wireOp",EDGE,"E329.filletArc"),sQuery(id+"F0.wireOp",EDGE,"E330.filletArc"),sQuery(id+"F0.wireOp",EDGE,"E331.filletArc"),sQuery(id+"F0.wireOp",EDGE,"E332.filletArc"),sQuery(id+"F0.wireOp",EDGE,"E333.filletArc"),sQuery(id+"F0.wireOp",EDGE,"E334.filletArc"),sQuery(id+"F0.wireOp",EDGE,"E335.filletArc"),sQuery(id+"F0.wireOp",EDGE,"E336.filletArc")])],"isStart":false});
            var sketch = newSketch(context, id + "F2", { "sketchPlane" : qUnion([Q0])});
            skLineSegment(sketch, "E337", {"start": v(-268.47, 155) * mm, "end": v(0, 310) * mm, "construction": true});
            skLineSegment(sketch, "E338", {"start": v(0, 310) * mm, "end": v(268.47, 155) * mm, "construction": true});
            skLineSegment(sketch, "E339", {"start": v(268.47, 155) * mm, "end": v(268.47, -155) * mm, "construction": true});
            skLineSegment(sketch, "E340", {"start": v(268.47, -155) * mm, "end": v(0, -310) * mm, "construction": true});
            skLineSegment(sketch, "E341", {"start": v(0, -310) * mm, "end": v(-268.47, -155) * mm, "construction": true});
            skLineSegment(sketch, "E342", {"start": v(-268.47, -155) * mm, "end": v(-268.47, 155) * mm, "construction": true});
            skCircle(sketch, "E343", {"center": v(0, 310) * mm, "radius": 5 * mm});
            skCircle(sketch, "E344", {"center": v(268.47, -155) * mm, "radius": 5 * mm});
            skCircle(sketch, "E345", {"center": v(0, -310) * mm, "radius": 5 * mm});
            skCircle(sketch, "E346", {"center": v(-268.47, -155) * mm, "radius": 5 * mm});
            skCircle(sketch, "E347", {"center": v(-268.47, 155) * mm, "radius": 5 * mm});
            skCircle(sketch, "E348", {"center": v(268.47, 155) * mm, "radius": 5 * mm});
            skCircle(sketch, "E349", {"center": v(0, 0) * mm, "radius": 391 * mm});
            skSolve(sketch);
        }
        {
            var Q0;
            Q0=makeQuery(id+"F2.imprint","IMPRINT",FACE,{"disambiguationData":[TD([[makeQuery(id+"F2.imprint","IMPRINT",EDGE,{"derivedFrom":sQuery(id+"F2.wireOp",EDGE,"E343")}),-1.0]])]});
            extrude(context, id + "F3", {"entities" : qUnion([Q0]), "operationType" : NewBodyOperationType.INTERSECT, "oppositeDirection" : true, "depth" : 5 * mm});
        }
    });
